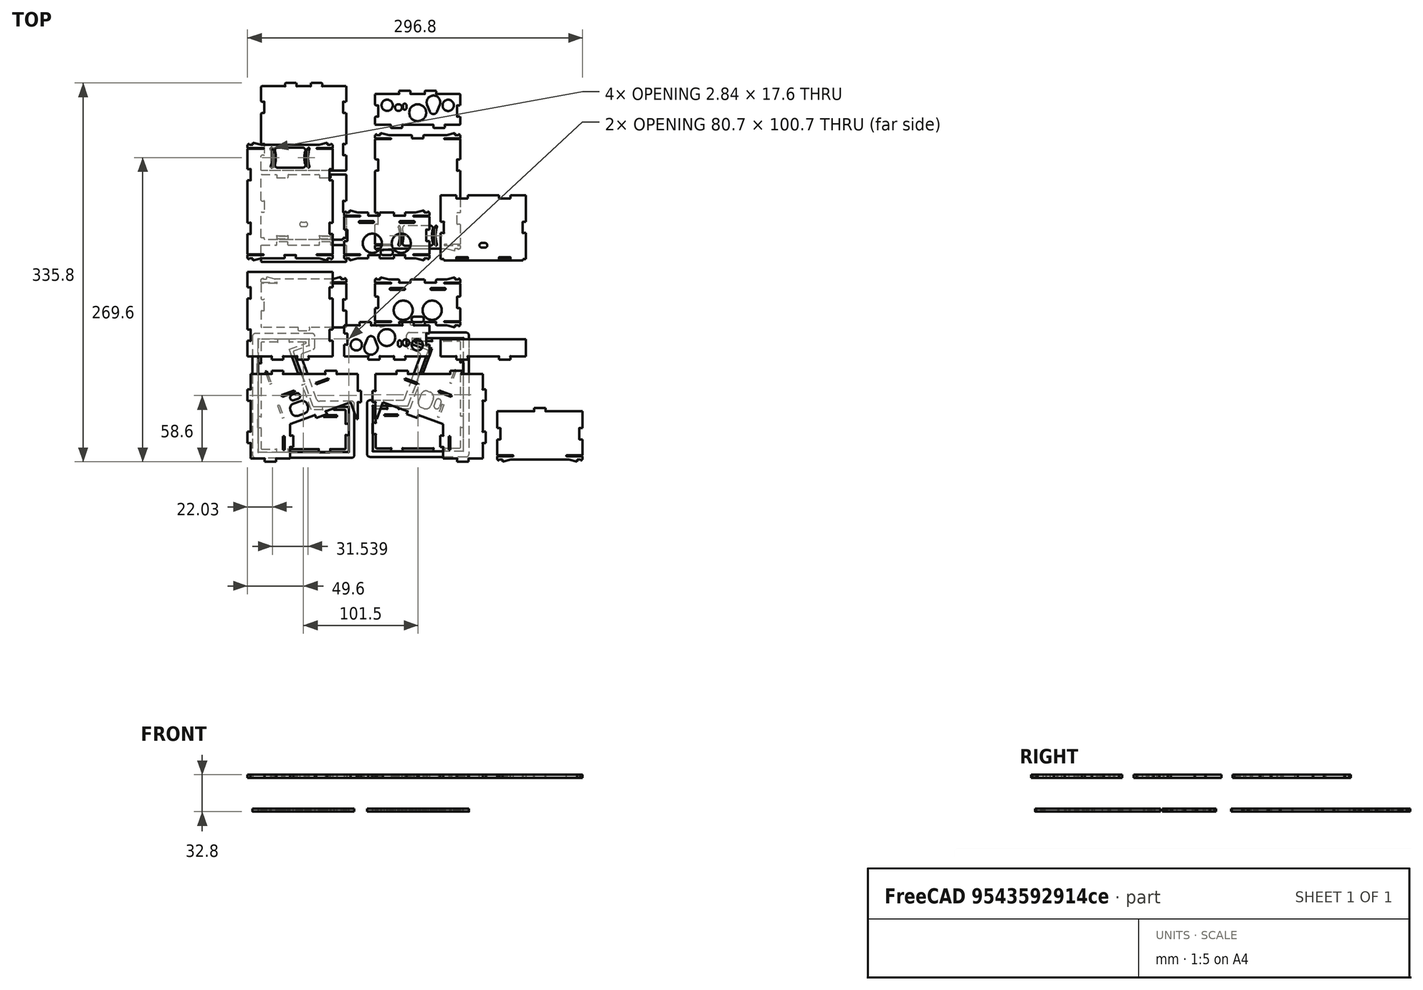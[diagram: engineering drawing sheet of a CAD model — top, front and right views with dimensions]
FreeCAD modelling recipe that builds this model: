
FCSTD DOCUMENT  (FreeCAD 1.0R39285 (Git))
Label: TheThing_v8_tabs_export_fix
License: CERN Open Hardware Licence permissive
LicenseURL: https://cern-ohl.web.cern.ch/
objects: Part::Part2DObjectPython×24, Part::Feature×11, Sketcher::SketchObject×10, Part::Chamfer×9, App::DocumentObjectGroup×2
note: 64 computed .brp shape members not serialized (recipe doc carries the construction recipe); baked Part::Feature solids carry a one-line shape summary decoded from their .brp

FEATURE [Part::Feature] test
  Placement = pos=(37.4,60.5,67.8) rot=(0,1,0;1.5708rad)
  shape: bbox 100.6 x 80.6 x 2.8 mm, 82 faces (baked)
FEATURE [Part::Feature] test001
  Placement = pos=(173.8,60.5,67.8) rot=(0,-1,0;1.5708rad)
  shape: bbox 100.6 x 80.6 x 2.8 mm, 70 faces (baked)
FEATURE [Part::Feature] test002
  Placement = pos=(259,27.5,93.2) rot=(0,-1,0;3.14159rad)
  shape: bbox 75.6 x 47.6 x 2.8 mm, 50 faces (baked)
FEATURE [Part::Feature] test003
  Placement = pos=(37.8,151.1,67.4) rot=(0,0,1;0rad)
  shape: bbox 75.6 x 77.8 x 2.8 mm, 42 faces (baked)
FEATURE [Part::Feature] test004
  Placement = pos=(123.4,151.1,33.2) rot=(0,-1,0;3.14159rad)
  shape: bbox 75.6 x 33.14 x 2.8 mm, 54 faces (baked)
FEATURE [Part::Feature] test005
  Placement = pos=(209,64.9222,78.0359) rot=(-0.34202,0,0;2.79253rad)
  shape: bbox 75.6 x 17.92 x 2.8 mm, 18 faces (baked)
FEATURE [Part::Feature] test006
  Placement = pos=(37.8,243.6,12.7) rot=(1,0,0;1.5708rad)
  shape: bbox 75.6 x 104.6 x 2.8 mm, 104 faces (baked)
FEATURE [Part::Feature] test007
  Placement = pos=(123.4,217.8,-27.7) rot=(-1,0,0;1.5708rad)
  shape: bbox 75.6 x 44.6 x 2.8 mm, 108 faces (baked)
FEATURE [Part::Feature] test008
  Placement = pos=(209,188.16,4.32219) rot=(-0.939693,0,0;1.22173rad)
  shape: bbox 75.6 x 58.11 x 2.925 mm, 56 faces (baked)
FEATURE [Part::Feature] test009
  Placement = pos=(171.3,46.5,-33) rot=(0.57735,0.57735,0.57735;4.18879rad)
  shape: bbox 90.2 x 110.2 x 2.8 mm, 46 faces (baked)
FEATURE [Part::Feature] test010
  Placement = pos=(29.4,45.7,-33) rot=(0.57735,-0.57735,-0.57735;4.18879rad)
  shape: bbox 90.2 x 110.2 x 2.8 mm, 46 faces (baked)
FEATURE [Part::Chamfer] Chamfer
  Base = -> test
  EdgeLinks = -> test [Edge25,Edge27,Edge39,Edge50,Edge52,Edge72,Edge74,Edge86,Edge97,Edge99,Edge119,Edge121,Edge133,Edge144,Edge146,Edge158,Edge169,Edge171,Edge194,Edge196]
  Edges = 20 edges r=0.5: [Edge25,Edge27,Edge39,Edge50,Edge52,Edge72,Edge74,Edge86,Edge97,Edge99,Edge119,Edge121,Edge133,Edge144,Edge146,Edge158,Edge169,Edge171,Edge194,Edge196]
  Placement = pos=(110.8,9.1,32.8) rot=(0.707107,0.707107,0;3.14159rad)
FEATURE [Part::Chamfer] Chamfer001
  Base = -> test001
  EdgeLinks = -> test001 [Edge25,Edge27,Edge39,Edge50,Edge52,Edge72,Edge74,Edge86,Edge97,Edge99,Edge119,Edge121,Edge133,Edge144,Edge146,Edge158,Edge169,Edge171,Edge194,Edge196]
  Edges = 20 edges r=0.5: [Edge25,Edge27,Edge39,Edge50,Edge52,Edge72,Edge74,Edge86,Edge97,Edge99,Edge119,Edge121,Edge133,Edge144,Edge146,Edge158,Edge169,Edge171,Edge194,Edge196]
  Placement = pos=(89.8,219.5,32.8) rot=(-0.707107,0.707107,0;3.14159rad)
FEATURE [Part::Chamfer] Chamfer002
  Base = -> test002
  EdgeLinks = -> test002 [Edge4,Edge6,Edge17,Edge20,Edge87,Edge103,Edge106,Edge120]
  Edges = 8 edges r=0.5: [Edge4,Edge6,Edge17,Edge20,Edge87,Edge103,Edge106,Edge120]
  Placement = pos=(308.8,163.8,-30) rot=(0,0,1;3.14159rad)
FEATURE [Part::Chamfer] Chamfer003
  Base = -> test003
  EdgeLinks = -> test003 [Edge1,Edge2,Edge7,Edge9,Edge27,Edge30,Edge45,Edge48,Edge59,Edge61,Edge81,Edge83,Edge95,Edge98,Edge121,Edge122]
  Edges = 16 edges r=0.5: [Edge1,Edge2,Edge7,Edge9,Edge27,Edge30,Edge45,Edge48,Edge59,Edge61,Edge81,Edge83,Edge95,Edge98,Edge121,Edge122]
  Placement = pos=(87.6,426.4,-30) rot=(0,0,1;3.14159rad)
FEATURE [Part::Chamfer] Chamfer004
  Base = -> test004
  EdgeLinks = -> test004 [Edge4,Edge7,Edge17,Edge20,Edge39,Edge42,Edge52,Edge55,Edge69,Edge73,Edge85,Edge88,Edge107,Edge110,Edge115,Edge123]
  Edges = 16 edges r=0.5: [Edge4,Edge7,Edge17,Edge20,Edge39,Edge42,Edge52,Edge55,Edge69,Edge73,Edge85,Edge88,Edge107,Edge110,Edge115,Edge123]
  Placement = pos=(274.2,419.6,-30) rot=(0,0,1;3.14159rad)
FEATURE [Part::Chamfer] Chamfer005
  Base = -> test005
  EdgeLinks = -> test005 [Edge1,Edge2,Edge5,Edge8,Edge28,Edge31,Edge50,Edge53]
  Edges = 8 edges r=0.5: [Edge1,Edge2,Edge5,Edge8,Edge28,Edge31,Edge50,Edge53]
  Placement = pos=(258.8,285.6,-30) rot=(0,0,1;3.14159rad)
FEATURE [Part::Chamfer] Chamfer006
  Base = -> test006
  EdgeLinks = -> test006 [Edge227,Edge232,Edge233,Edge238,Edge267,Edge272,Edge273,Edge278,Edge293,Edge298]
  Edges = 10 edges r=0.5: [Edge227,Edge232,Edge233,Edge238,Edge267,Edge272,Edge273,Edge278,Edge293,Edge298]
  Placement = pos=(188.6,470,-30) rot=(0,0,1;3.14159rad)
FEATURE [Part::Chamfer] Chamfer007
  Base = -> test007
  EdgeLinks = -> test007 [Edge243,Edge248,Edge249,Edge254,Edge269,Edge274,Edge289,Edge294,Edge295,Edge300,Edge315,Edge320]
  Edges = 12 edges r=0.5: [Edge243,Edge248,Edge249,Edge254,Edge269,Edge274,Edge289,Edge294,Edge295,Edge300,Edge315,Edge320]
  Placement = pos=(27.4,-59.4,-30) rot=(0,0,1;0rad)
FEATURE [Part::Chamfer] Chamfer008
  Base = -> test008
  EdgeLinks = -> test008 [Edge2,Edge4,Edge104,Edge105,Edge107,Edge118,Edge142,Edge143,Edge148,Edge149,Edge150,Edge155,Edge156,Edge164]
  Edges = 14 edges r=0.5: [Edge2,Edge4,Edge104,Edge105,Edge107,Edge118,Edge142,Edge143,Edge148,Edge149,Edge150,Edge155,Edge156,Edge164]
  Placement = pos=(-159.2,18.6,-30) rot=(0,0,1;0rad)
FEATURE [Sketcher::SketchObject] Sketch
  ArcFitTolerance = 1e-06
  FullyConstrained = true
  MakeInternals = false
  sketch-geometry (52):
    g0: LineSegment StartX=5 StartY=0 StartZ=0 EndX=95 EndY=0 EndZ=0
    g1: LineSegment StartX=100 StartY=5 StartZ=0 EndX=100 EndY=165 EndZ=0
    g2: LineSegment StartX=95 StartY=170 StartZ=0 EndX=5 EndY=170 EndZ=0
    g3: LineSegment StartX=0 StartY=165 StartZ=0 EndX=0 EndY=5 EndZ=0
    g4: LineSegment StartX=5 StartY=171 StartZ=0 EndX=95 EndY=171 EndZ=0
    g5: LineSegment StartX=100 StartY=176 StartZ=0 EndX=100 EndY=336 EndZ=0
    g6: LineSegment StartX=95 StartY=341 StartZ=0 EndX=5 EndY=341 EndZ=0
    g7: LineSegment StartX=0 StartY=336 StartZ=0 EndX=0 EndY=176 EndZ=0
    g8: LineSegment StartX=106 StartY=171 StartZ=0 EndX=196 EndY=171 EndZ=0
    g9: LineSegment StartX=201 StartY=176 StartZ=0 EndX=201 EndY=336 EndZ=0
    g10: LineSegment StartX=196 StartY=341 StartZ=0 EndX=106 EndY=341 EndZ=0
    g11: LineSegment StartX=101 StartY=336 StartZ=0 EndX=101 EndY=176 EndZ=0
    g12: LineSegment StartX=106 StartY=0 StartZ=0 EndX=196 EndY=0 EndZ=0
    g13: LineSegment StartX=201 StartY=5 StartZ=0 EndX=201 EndY=165 EndZ=0
    g14: LineSegment StartX=196 StartY=170 StartZ=0 EndX=106 EndY=170 EndZ=0
    g15: LineSegment StartX=101 StartY=165 StartZ=0 EndX=101 EndY=5 EndZ=0
    g16: LineSegment [constr] StartX=100 StartY=170 StartZ=0 EndX=101 EndY=170 EndZ=0
    g17: LineSegment [constr] StartX=101 StartY=170 StartZ=0 EndX=101 EndY=171 EndZ=0
    g18: LineSegment [constr] StartX=101 StartY=171 StartZ=0 EndX=100 EndY=171 EndZ=0
    g19: LineSegment [constr] StartX=100 StartY=171 StartZ=0 EndX=100 EndY=170 EndZ=0
    g20: ArcOfCircle CenterX=5 CenterY=5 CenterZ=0 NormalX=0 NormalY=0 NormalZ=1 AngleXU=0 Radius=5 StartAngle=3.14159 EndAngle=4.71239
    g21: GeomPoint [constr] X=0 Y=0 Z=0
    g22: ArcOfCircle CenterX=95 CenterY=5 CenterZ=0 NormalX=0 NormalY=0 NormalZ=1 AngleXU=0 Radius=5 StartAngle=4.71239 EndAngle=6.28319
    g23: GeomPoint [constr] X=100 Y=0 Z=0
    g24: ArcOfCircle CenterX=106 CenterY=5 CenterZ=0 NormalX=0 NormalY=0 NormalZ=1 AngleXU=0 Radius=5 StartAngle=3.14159 EndAngle=4.71239
    g25: GeomPoint [constr] X=101 Y=0 Z=0
    g26: ArcOfCircle CenterX=196 CenterY=5 CenterZ=0 NormalX=0 NormalY=0 NormalZ=1 AngleXU=0 Radius=5 StartAngle=4.71239 EndAngle=6.28319
    g27: GeomPoint [constr] X=201 Y=0 Z=0
    g28: ArcOfCircle CenterX=95 CenterY=176 CenterZ=0 NormalX=0 NormalY=0 NormalZ=1 AngleXU=0 Radius=5 StartAngle=4.71239 EndAngle=6.28319
    g29: GeomPoint [constr] X=100 Y=171 Z=0
    g30: ArcOfCircle CenterX=95 CenterY=165 CenterZ=0 NormalX=0 NormalY=0 NormalZ=1 AngleXU=0 Radius=5 StartAngle=3e-16 EndAngle=1.5708
    g31: GeomPoint [constr] X=100 Y=170 Z=0
    g32: ArcOfCircle CenterX=106 CenterY=165 CenterZ=0 NormalX=0 NormalY=0 NormalZ=1 AngleXU=0 Radius=5 StartAngle=1.5708 EndAngle=3.14159
    g33: GeomPoint [constr] X=101 Y=170 Z=0
    g34: ArcOfCircle CenterX=106 CenterY=176 CenterZ=0 NormalX=0 NormalY=0 NormalZ=1 AngleXU=0 Radius=5 StartAngle=3.14159 EndAngle=4.71239
    g35: GeomPoint [constr] X=101 Y=171 Z=0
    g36: ArcOfCircle CenterX=5 CenterY=176 CenterZ=0 NormalX=0 NormalY=0 NormalZ=1 AngleXU=0 Radius=5 StartAngle=3.14159 EndAngle=4.71239
    g37: GeomPoint [constr] X=0 Y=171 Z=0
    g38: ArcOfCircle CenterX=196 CenterY=176 CenterZ=0 NormalX=0 NormalY=0 NormalZ=1 AngleXU=0 Radius=5 StartAngle=4.71239 EndAngle=6.28319
    g39: GeomPoint [constr] X=201 Y=171 Z=0
    g40: ArcOfCircle CenterX=196 CenterY=165 CenterZ=0 NormalX=0 NormalY=0 NormalZ=1 AngleXU=0 Radius=5 StartAngle=2.4e-15 EndAngle=1.5708
    g41: GeomPoint [constr] X=201 Y=170 Z=0
    g42: ArcOfCircle CenterX=5 CenterY=165 CenterZ=0 NormalX=0 NormalY=0 NormalZ=1 AngleXU=0 Radius=5 StartAngle=1.5708 EndAngle=3.14159
    g43: GeomPoint [constr] X=0 Y=170 Z=0
    g44: ArcOfCircle CenterX=5 CenterY=336 CenterZ=0 NormalX=0 NormalY=0 NormalZ=1 AngleXU=0 Radius=5 StartAngle=1.5708 EndAngle=3.14159
    g45: GeomPoint [constr] X=0 Y=341 Z=0
    g46: ArcOfCircle CenterX=95 CenterY=336 CenterZ=0 NormalX=0 NormalY=0 NormalZ=1 AngleXU=0 Radius=5 StartAngle=1.7e-15 EndAngle=1.5708
    g47: GeomPoint [constr] X=100 Y=341 Z=0
    g48: ArcOfCircle CenterX=106 CenterY=336 CenterZ=0 NormalX=0 NormalY=0 NormalZ=1 AngleXU=0 Radius=5 StartAngle=1.5708 EndAngle=3.14159
    g49: GeomPoint [constr] X=101 Y=341 Z=0
    g50: ArcOfCircle CenterX=196 CenterY=336 CenterZ=0 NormalX=0 NormalY=0 NormalZ=1 AngleXU=0 Radius=5 StartAngle=-2.7e-15 EndAngle=1.5708
    g51: GeomPoint [constr] X=201 Y=341 Z=0
  constraints (119):
    c: Horizontal(g0)
    c: Horizontal(g2)
    c: Vertical(g1)
    c: Vertical(g3)
    c: Coincident(g21,g-1)
    c: Horizontal(g4)
    c: Horizontal(g6)
    c: Vertical(g5)
    c: Vertical(g7)
    c: Horizontal(g8)
    c: Horizontal(g10)
    c: Vertical(g9)
    c: Vertical(g11)
    c: Horizontal(g12)
    c: Horizontal(g14)
    c: Vertical(g13)
    c: Vertical(g15)
    c: DistanceX(g21,g23) = 100
    c: DistanceY(g21,g43) = 170
    c: Coincident(g16,g17)
    c: Coincident(g17,g18)
    c: Coincident(g18,g19)
    c: Coincident(g19,g16)
    c: Horizontal(g16)
    c: Horizontal(g18)
    c: Vertical(g17)
    c: Vertical(g19)
    c: Distance(g17,g19) = 1
    c: Distance(g16,g18) = 1
    c: Coincident(g16,g31)
    c: Coincident(g18,g29)
    c: Coincident(g17,g35)
    c: Coincident(g16,g33)
    c: PointOnObject(g21,g0)
    c: PointOnObject(g21,g3)
    c: Tangent(g0,g20) = -1.5708
    c: Tangent(g3,g20) = -1.5708
    c: PointOnObject(g23,g0)
    c: PointOnObject(g23,g1)
    c: Tangent(g0,g22) = -1.5708
    c: Tangent(g1,g22) = -1.5708
    c: PointOnObject(g25,g12)
    c: PointOnObject(g25,g15)
    c: Tangent(g12,g24) = -1.5708
    c: Tangent(g15,g24) = -1.5708
    c: PointOnObject(g27,g13)
    c: PointOnObject(g27,g12)
    c: Tangent(g13,g26) = -1.5708
    c: Tangent(g12,g26) = -1.5708
    c: PointOnObject(g29,g5)
    c: PointOnObject(g29,g4)
    c: Tangent(g5,g28) = -1.5708
    c: Tangent(g4,g28) = -1.5708
    c: PointOnObject(g31,g2)
    c: PointOnObject(g31,g1)
    c: Tangent(g2,g30) = -1.5708
    c: Tangent(g1,g30) = -1.5708
    c: PointOnObject(g33,g14)
    c: PointOnObject(g33,g15)
    c: Tangent(g14,g32) = -1.5708
    c: Tangent(g15,g32) = -1.5708
    c: PointOnObject(g35,g8)
    c: PointOnObject(g35,g11)
    c: Tangent(g8,g34) = -1.5708
    c: Tangent(g11,g34) = -1.5708
    c: PointOnObject(g37,g4)
    c: PointOnObject(g37,g7)
    c: Tangent(g4,g36) = -1.5708
    c: Tangent(g7,g36) = -1.5708
    c: PointOnObject(g39,g8)
    c: PointOnObject(g39,g9)
    c: Tangent(g8,g38) = -1.5708
    c: Tangent(g9,g38) = -1.5708
    c: PointOnObject(g41,g14)
    c: PointOnObject(g41,g13)
    c: Tangent(g14,g40) = -1.5708
    c: Tangent(g13,g40) = -1.5708
    c: PointOnObject(g43,g2)
    c: PointOnObject(g43,g3)
    c: Tangent(g2,g42) = -1.5708
    c: Tangent(g3,g42) = -1.5708
    c: PointOnObject(g45,g6)
    c: PointOnObject(g45,g7)
    c: Tangent(g6,g44) = -1.5708
    c: Tangent(g7,g44) = -1.5708
    c: PointOnObject(g47,g6)
    c: PointOnObject(g47,g5)
    c: Tangent(g6,g46) = -1.5708
    c: Tangent(g5,g46) = -1.5708
    c: PointOnObject(g49,g10)
    c: PointOnObject(g49,g11)
    c: Tangent(g10,g48) = -1.5708
    c: Tangent(g11,g48) = -1.5708
    c: PointOnObject(g51,g10)
    c: PointOnObject(g51,g9)
    c: Tangent(g10,g50) = -1.5708
    c: Tangent(g9,g50) = -1.5708
    c: Equal(g50,g48)
    c: Equal(g48,g46)
    c: Equal(g46,g44)
    c: Equal(g44,g36)
    c: Equal(g36,g42)
    c: Equal(g42,g28)
    c: Equal(g28,g34)
    c: Equal(g34,g32)
    c: Equal(g32,g30)
    c: Equal(g30,g38)
    c: Equal(g38,g40)
    c: Equal(g40,g26)
    c: Equal(g26,g24)
    c: Equal(g24,g22)
    c: Equal(g22,g20)
    c: Radius(g20) = 5
    c: Vertical(g37,g43)
    c: Horizontal(g25,g23)
    c: Vertical(g39,g41)
    c: Horizontal(g47,g49)
    c: Equal(g7,g3)
    c: Equal(g6,g10)
FEATURE [Part::Part2DObjectPython] Shape2DView  # Draft 2D object (typed FeaturePython)
  AutoUpdate = true
  Clip = false
  FuseArch = false
  HiddenLines = false
  InPlace = true
  OnlySolids = false
  Placement = pos=(96,354,3) rot=(0,0,1;1.5708rad)
  Projection = (-0.0061258,0.0189136,0.999802)
  ProjectionMode = 0
  SegmentLength = 0.05
  Tessellation = false
  VisibleOnly = false
FEATURE [Part::Part2DObjectPython] Shape2DView001  # Draft 2D object (typed FeaturePython)
  AutoUpdate = true
  Clip = false
  FuseArch = false
  HiddenLines = false
  InPlace = true
  OnlySolids = false
  Placement = pos=(138,7,3) rot=(0,0,1;3.14159rad)
  Projection = (0,0,1)
  ProjectionMode = 0
  SegmentLength = 0.05
  Tessellation = false
  VisibleOnly = false
FEATURE [Part::Part2DObjectPython] Shape2DView002  # Draft 2D object (typed FeaturePython)
  AutoUpdate = true
  Base = -> Chamfer008
  Clip = false
  FuseArch = false
  HiddenLines = false
  InPlace = true
  OnlySolids = false
  Projection = (0,0,1)
  ProjectionMode = 0
  SegmentLength = 0.05
  Tessellation = false
  VisibleOnly = false
FEATURE [Sketcher::SketchObject] Sketch001
  ArcFitTolerance = 1e-06
  FullyConstrained = false
  MakeInternals = false
  sketch-geometry (78):
    g0: LineSegment StartX=12.5 StartY=254.796 StartZ=0 EndX=25.425 EndY=254.796 EndZ=0
    g1: LineSegment StartX=14.8 StartY=198.4 StartZ=0 EndX=12.5 EndY=198.4 EndZ=0
    g2: LineSegment StartX=12.5 StartY=198.4 StartZ=0 EndX=12 EndY=198.9 EndZ=0
    g3: LineSegment StartX=14.8 StartY=197.5 StartZ=0 EndX=14.8 EndY=198.4 EndZ=0
    g4: LineSegment StartX=12 StartY=198.9 StartZ=0 EndX=12 EndY=220.843 EndZ=0
    g5: LineSegment StartX=14.8 StartY=197.5 StartZ=0 EndX=15.3 EndY=197 EndZ=0
    g6: LineSegment StartX=12.5 StartY=221.343 StartZ=0 EndX=12 EndY=220.843 EndZ=0
    g7: LineSegment StartX=25.4273 StartY=197.002 StartZ=0 EndX=15.3 EndY=197.002 EndZ=0
    g8: LineSegment StartX=12.5 StartY=221.343 StartZ=0 EndX=14.5913 EndY=221.343 EndZ=0
    g9: ArcOfCircle CenterX=14.7648 CenterY=221.443 CenterZ=0 NormalX=0 NormalY=0 NormalZ=1 AngleXU=0 Radius=0.200333 StartAngle=3.66519 EndAngle=6.28319
    g10: LineSegment StartX=25.925 StartY=199.585 StartZ=0 EndX=25.925 EndY=197.5 EndZ=0
    g11: ArcOfCircle CenterX=14.7648 CenterY=221.443 CenterZ=0 NormalX=0 NormalY=0 NormalZ=1 AngleXU=0 Radius=0.200333 StartAngle=0 EndAngle=1.0472
    g12: ArcOfEllipse CenterX=26.0227 CenterY=199.765 CenterZ=0 NormalX=0 NormalY=0 NormalZ=1 MajorRadius=0.207869 MinorRadius=0.195333 AngleXU=1.5708 StartAngle=1.5708 EndAngle=2.61799
    g13: ArcOfEllipse CenterX=26.0227 CenterY=199.765 CenterZ=0 NormalX=0 NormalY=0 NormalZ=1 MajorRadius=0.207869 MinorRadius=0.195333 AngleXU=1.5708 StartAngle=5.23599 EndAngle=7.85398
    g14: LineSegment StartX=14.865 StartY=231.019 StartZ=0 EndX=14.865 EndY=221.616 EndZ=0
    g15: LineSegment StartX=35.6082 StartY=199.869 StartZ=0 EndX=26.1918 EndY=199.869 EndZ=0
    g16: ArcOfCircle CenterX=14.7648 CenterY=231.192 CenterZ=0 NormalX=0 NormalY=0 NormalZ=1 AngleXU=0 Radius=0.200333 StartAngle=5.23599 EndAngle=6.28319
    g17: ArcOfEllipse CenterX=35.7773 CenterY=199.765 CenterZ=0 NormalX=0 NormalY=0 NormalZ=1 MajorRadius=0.207869 MinorRadius=0.195333 AngleXU=1.5708 StartAngle=4.71239 EndAngle=7.33038
    g18: ArcOfEllipse CenterX=35.7773 CenterY=199.765 CenterZ=0 NormalX=0 NormalY=0 NormalZ=1 MajorRadius=0.207869 MinorRadius=0.195333 AngleXU=1.5708 StartAngle=3.66519 EndAngle=4.71239
    g19: ArcOfCircle CenterX=14.7648 CenterY=231.192 CenterZ=0 NormalX=0 NormalY=0 NormalZ=1 AngleXU=0 Radius=0.200333 StartAngle=0 EndAngle=2.61799
    g20: LineSegment StartX=35.875 StartY=199.585 StartZ=0 EndX=35.875 EndY=197.5 EndZ=0
    g21: LineSegment StartX=12.5 StartY=231.293 StartZ=0 EndX=14.5913 EndY=231.293 EndZ=0
    g22: LineSegment StartX=12 StartY=231.793 StartZ=0 EndX=12.5 EndY=231.293 EndZ=0
    g23: LineSegment StartX=63.2283 StartY=197.003 StartZ=0 EndX=36.3717 EndY=197.003 EndZ=0
    g24: LineSegment StartX=12.5 StartY=254.796 StartZ=0 EndX=12 EndY=254.296 EndZ=0
    g25: LineSegment StartX=63.725 StartY=199.585 StartZ=0 EndX=63.725 EndY=197.5 EndZ=0
    g26: ArcOfEllipse CenterX=63.8227 CenterY=199.765 CenterZ=0 NormalX=0 NormalY=0 NormalZ=1 MajorRadius=0.207869 MinorRadius=0.195333 AngleXU=1.5708 StartAngle=1.5708 EndAngle=2.61799
    g27: ArcOfEllipse CenterX=63.8227 CenterY=199.765 CenterZ=0 NormalX=0 NormalY=0 NormalZ=1 MajorRadius=0.207869 MinorRadius=0.195333 AngleXU=1.5708 StartAngle=5.23599 EndAngle=7.85398
    g28: LineSegment StartX=25.425 StartY=254.796 StartZ=0 EndX=25.925 EndY=254.296 EndZ=0
    g29: LineSegment StartX=73.4082 StartY=199.869 StartZ=0 EndX=63.9918 EndY=199.869 EndZ=0
    g30: LineSegment StartX=25.925 StartY=254.296 StartZ=0 EndX=25.925 EndY=252.204 EndZ=0
    g31: ArcOfEllipse CenterX=73.5773 CenterY=199.765 CenterZ=0 NormalX=0 NormalY=0 NormalZ=1 MajorRadius=0.207869 MinorRadius=0.195333 AngleXU=1.5708 StartAngle=4.71239 EndAngle=7.33038
    g32: ArcOfEllipse CenterX=73.5773 CenterY=199.765 CenterZ=0 NormalX=0 NormalY=0 NormalZ=1 MajorRadius=0.207869 MinorRadius=0.195333 AngleXU=1.5708 StartAngle=3.66519 EndAngle=4.71239
    g33: ArcOfCircle CenterX=26.0252 CenterY=252.031 CenterZ=0 NormalX=0 NormalY=0 NormalZ=1 AngleXU=-1.5708 Radius=0.200333 StartAngle=3.66519 EndAngle=6.28319
    g34: LineSegment StartX=73.675 StartY=199.585 StartZ=0 EndX=73.675 EndY=197.5 EndZ=0
    g35: ArcOfCircle CenterX=26.0252 CenterY=252.031 CenterZ=0 NormalX=0 NormalY=0 NormalZ=1 AngleXU=-1.5708 Radius=0.200333 StartAngle=0 EndAngle=1.0472
    g36: LineSegment StartX=26.1987 StartY=251.931 StartZ=0 EndX=35.6013 EndY=251.931 EndZ=0
    g37: LineSegment StartX=84.3 StartY=196.999 StartZ=0 EndX=74.1757 EndY=196.999 EndZ=0
    g38: ArcOfCircle CenterX=35.7748 CenterY=252.031 CenterZ=0 NormalX=0 NormalY=0 NormalZ=1 AngleXU=-1.5708 Radius=0.200333 StartAngle=5.23599 EndAngle=6.28319
    g39: LineSegment StartX=84.3 StartY=197 StartZ=0 EndX=84.8 EndY=197.5 EndZ=0
    g40: ArcOfCircle CenterX=35.7748 CenterY=252.031 CenterZ=0 NormalX=0 NormalY=0 NormalZ=1 AngleXU=-1.5708 Radius=0.200333 StartAngle=0 EndAngle=2.61799
    g41: LineSegment StartX=84.8 StartY=198.4 StartZ=0 EndX=84.8 EndY=197.5 EndZ=0
    g42: LineSegment StartX=35.875 StartY=254.296 StartZ=0 EndX=35.875 EndY=252.204 EndZ=0
    g43: LineSegment StartX=87.1 StartY=198.4 StartZ=0 EndX=84.8 EndY=198.4 EndZ=0
    g44: LineSegment StartX=36.375 StartY=254.796 StartZ=0 EndX=35.875 EndY=254.296 EndZ=0
    g45: LineSegment StartX=87.1 StartY=198.4 StartZ=0 EndX=87.6 EndY=198.9 EndZ=0
    g46: LineSegment StartX=36.375 StartY=254.796 StartZ=0 EndX=63.225 EndY=254.796 EndZ=0
    g47: LineSegment StartX=87.6 StartY=220.843 StartZ=0 EndX=87.6 EndY=198.9 EndZ=0
    g48: LineSegment StartX=63.725 StartY=254.296 StartZ=0 EndX=63.225 EndY=254.796 EndZ=0
    g49: LineSegment StartX=87.6 StartY=220.843 StartZ=0 EndX=87.1 EndY=221.343 EndZ=0
    g50: LineSegment StartX=63.725 StartY=254.296 StartZ=0 EndX=63.725 EndY=252.204 EndZ=0
    g51: LineSegment StartX=85.0087 StartY=221.343 StartZ=0 EndX=87.1 EndY=221.343 EndZ=0
    g52: ArcOfCircle CenterX=63.8252 CenterY=252.031 CenterZ=0 NormalX=0 NormalY=0 NormalZ=1 AngleXU=-1.5708 Radius=0.200333 StartAngle=3.66519 EndAngle=6.28319
    g53: ArcOfCircle CenterX=84.8352 CenterY=221.443 CenterZ=0 NormalX=0 NormalY=0 NormalZ=1 AngleXU=0 Radius=0.200333 StartAngle=2.0944 EndAngle=5.75959
    g54: ArcOfCircle CenterX=63.8252 CenterY=252.031 CenterZ=0 NormalX=0 NormalY=0 NormalZ=1 AngleXU=-1.5708 Radius=0.200333 StartAngle=0 EndAngle=1.0472
    g55: LineSegment StartX=84.735 StartY=231.019 StartZ=0 EndX=84.735 EndY=221.616 EndZ=0
    g56: LineSegment StartX=63.9987 StartY=251.931 StartZ=0 EndX=73.4013 EndY=251.931 EndZ=0
    g57: ArcOfCircle CenterX=84.8352 CenterY=231.192 CenterZ=0 NormalX=0 NormalY=0 NormalZ=1 AngleXU=0 Radius=0.200333 StartAngle=0.523599 EndAngle=4.18879
    g58: ArcOfCircle CenterX=73.5748 CenterY=252.031 CenterZ=0 NormalX=0 NormalY=0 NormalZ=1 AngleXU=-1.5708 Radius=0.200333 StartAngle=5.23599 EndAngle=6.28319
    g59: LineSegment StartX=85.0087 StartY=231.293 StartZ=0 EndX=87.1 EndY=231.293 EndZ=0
    g60: ArcOfCircle CenterX=73.5748 CenterY=252.031 CenterZ=0 NormalX=0 NormalY=0 NormalZ=1 AngleXU=-1.5708 Radius=0.200333 StartAngle=0 EndAngle=2.61799
    g61: LineSegment StartX=87.1 StartY=231.293 StartZ=0 EndX=87.6 EndY=231.793 EndZ=0
    g62: LineSegment StartX=73.675 StartY=254.296 StartZ=0 EndX=73.675 EndY=252.204 EndZ=0
    g63: LineSegment StartX=74.175 StartY=254.796 StartZ=0 EndX=73.675 EndY=254.296 EndZ=0
    g64: LineSegment StartX=87.6 StartY=254.296 StartZ=0 EndX=87.1 EndY=254.796 EndZ=0
    g65: LineSegment StartX=74.175 StartY=254.796 StartZ=0 EndX=87.1 EndY=254.796 EndZ=0
    g66: LineSegment StartX=48.3 StartY=212.512 StartZ=0 EndX=51.3 EndY=212.512 EndZ=0
    g67: ArcOfCircle CenterX=48.3 CenterY=210.512 CenterZ=0 NormalX=0 NormalY=0 NormalZ=1 AngleXU=0 Radius=2 StartAngle=1.5708 EndAngle=4.71239
    g68: ArcOfCircle CenterX=51.3 CenterY=210.512 CenterZ=0 NormalX=0 NormalY=0 NormalZ=1 AngleXU=0 Radius=2 StartAngle=4.71239 EndAngle=7.85398
    g69: LineSegment StartX=48.3 StartY=208.512 StartZ=0 EndX=51.3 EndY=208.512 EndZ=0
    g70: LineSegment StartX=12 StartY=254.296 StartZ=0 EndX=12 EndY=233.023 EndZ=0
    g71: LineSegment StartX=12 StartY=231.793 StartZ=0 EndX=12 EndY=232.027 EndZ=0
    g72: LineSegment StartX=87.6 StartY=231.793 StartZ=0 EndX=87.6 EndY=232.021 EndZ=0
    g73: LineSegment StartX=87.6 StartY=233.009 StartZ=0 EndX=87.6 EndY=254.296 EndZ=0
    g74: LineSegment StartX=25.925 StartY=197.5 StartZ=0 EndX=25.4273 EndY=197.002 EndZ=0
    g75: LineSegment StartX=35.875 StartY=197.5 StartZ=0 EndX=36.3717 EndY=197.003 EndZ=0
    g76: LineSegment StartX=63.725 StartY=197.5 StartZ=0 EndX=63.2283 EndY=197.003 EndZ=0
    g77: LineSegment StartX=73.675 StartY=197.5 StartZ=0 EndX=74.1757 EndY=196.999 EndZ=0
  constraints (32):
    c: Coincident(g70,g24)
    c: Vertical(g70)
    c: Coincident(g71,g22)
    c: Vertical(g71)
    c: Coincident(g11,g14)
    c: Vertical(g55)
    c: Vertical(g14)
    c: Coincident(g72,g61)
    c: Vertical(g72)
    c: Coincident(g73,g64)
    c: Vertical(g73)
    c: Horizontal(g7)
    c: Vertical(g10)
    c: Vertical(g20)
    c: Horizontal(g23)
    c: Vertical(g25)
    c: Vertical(g34)
    c: Horizontal(g37)
    c: DistanceX(g3) = 14.8
    c: DistanceY(g3) = 197.5
    c: Angle(g-1,g74) = -2.35619
    c: Angle(g-1,g75) = -0.785398
    c: Angle(g-1,g76) = -2.35619
    c: Angle(g-1,g77) = -0.785398
    c: Coincident(g23,g76)
    c: PointOnObject(g25,g76)
    c: Coincident(g37,g77)
    c: Coincident(g34,g77)
    c: PointOnObject(g20,g75)
    c: Coincident(g23,g75)
    c: Coincident(g7,g74)
    c: Coincident(g10,g74)
FEATURE [Part::Part2DObjectPython] Shape2DView003  # Draft 2D object (typed FeaturePython)
  AutoUpdate = true
  Base = -> test009
  Clip = false
  FuseArch = false
  HiddenLines = false
  InPlace = true
  OnlySolids = false
  Projection = (0,0,1)
  ProjectionMode = 0
  SegmentLength = 0.05
  Tessellation = false
  VisibleOnly = false
FEATURE [Part::Part2DObjectPython] Shape2DView004  # Draft 2D object (typed FeaturePython)
  AutoUpdate = true
  Base = -> test010
  Clip = false
  FuseArch = false
  HiddenLines = false
  InPlace = true
  OnlySolids = false
  Placement = pos=(0,1,0) rot=(0,0,1;0rad)
  Projection = (0,0,1)
  ProjectionMode = 0
  SegmentLength = 0.05
  Tessellation = false
  VisibleOnly = false
FEATURE [Part::Part2DObjectPython] Shape2DView005  # Draft 2D object (typed FeaturePython)
  AutoUpdate = true
  Base = -> Chamfer
  Clip = false
  FuseArch = false
  HiddenLines = false
  InPlace = true
  OnlySolids = false
  Projection = (0,0,1)
  ProjectionMode = 0
  SegmentLength = 0.05
  Tessellation = false
  VisibleOnly = false
FEATURE [Part::Part2DObjectPython] Shape2DView006  # Draft 2D object (typed FeaturePython)
  AutoUpdate = true
  Base = -> Chamfer001
  Clip = false
  FuseArch = false
  HiddenLines = false
  InPlace = true
  OnlySolids = false
  Placement = pos=(0,1,0) rot=(0,0,1;0rad)
  Projection = (0,0,1)
  ProjectionMode = 0
  SegmentLength = 0.05
  Tessellation = false
  VisibleOnly = false
FEATURE [Part::Part2DObjectPython] Shape2DView007  # Draft 2D object (typed FeaturePython)
  AutoUpdate = true
  Base = -> Chamfer002
  Clip = false
  FuseArch = false
  HiddenLines = false
  InPlace = true
  OnlySolids = false
  Projection = (0,0,1)
  ProjectionMode = 0
  SegmentLength = 0.05
  Tessellation = false
  VisibleOnly = false
FEATURE [Part::Part2DObjectPython] Shape2DView008  # Draft 2D object (typed FeaturePython)
  AutoUpdate = true
  Base = -> Chamfer003
  Clip = false
  FuseArch = false
  HiddenLines = false
  InPlace = true
  OnlySolids = false
  Projection = (0,0,1)
  ProjectionMode = 0
  SegmentLength = 0.05
  Tessellation = false
  VisibleOnly = false
FEATURE [Part::Part2DObjectPython] Shape2DView009  # Draft 2D object (typed FeaturePython)
  AutoUpdate = true
  Base = -> Chamfer004
  Clip = false
  FuseArch = false
  HiddenLines = false
  InPlace = true
  OnlySolids = false
  Projection = (0,0,1)
  ProjectionMode = 0
  SegmentLength = 0.05
  Tessellation = false
  VisibleOnly = false
FEATURE [Part::Part2DObjectPython] Shape2DView010  # Draft 2D object (typed FeaturePython)
  AutoUpdate = true
  Base = -> Chamfer005
  Clip = false
  FuseArch = false
  HiddenLines = false
  InPlace = true
  OnlySolids = false
  Projection = (0,0,1)
  ProjectionMode = 0
  SegmentLength = 0.05
  Tessellation = false
  VisibleOnly = false
FEATURE [Part::Part2DObjectPython] Shape2DView011  # Draft 2D object (typed FeaturePython)
  AutoUpdate = true
  Base = -> Chamfer006
  Clip = false
  FuseArch = false
  HiddenLines = false
  InPlace = true
  OnlySolids = false
  Projection = (0,0,1)
  ProjectionMode = 0
  SegmentLength = 0.05
  Tessellation = false
  VisibleOnly = false
FEATURE [Part::Part2DObjectPython] Shape2DView012  # Draft 2D object (typed FeaturePython)
  AutoUpdate = true
  Base = -> Chamfer007
  Clip = false
  FuseArch = false
  HiddenLines = false
  InPlace = true
  OnlySolids = false
  Projection = (0,0,1)
  ProjectionMode = 0
  SegmentLength = 0.05
  Tessellation = false
  VisibleOnly = false
FEATURE [App::DocumentObjectGroup] Group  label="Incoming_Solids"
  Group = -> [test009,test010,Chamfer,Chamfer001,Chamfer002,Chamfer003,Chamfer004,Chamfer005,Chamfer006,Chamfer007,Chamfer008,Shape2DView002,Shape2DView003,Shape2DView004,Shape2DView005,Shape2DView006,Shape2DView007,Shape2DView008,Shape2DView009,Shape2DView010,Shape2DView011,Shape2DView012]
FEATURE [Part::Part2DObjectPython] ShapeString  # Draft 2D object (typed FeaturePython)
  FontFile = <userpath>/Downloads/fonts/Droid_Sans_Mono/DroidSansMono.ttf
  Fuse = false
  Justification = 6
  JustificationReference = 0
  KeepLeftMargin = false
  MakeFace = true
  ObliqueAngle = 0
  Placement = pos=(166,103,0) rot=(0,0,1;0rad)
  ScaleToSize = true
  Size = 2.5
  String = [1]
  Tracking = 0
FEATURE [Part::Part2DObjectPython] ShapeString001  # Draft 2D object (typed FeaturePython)
  FontFile = <userpath>/Downloads/fonts/Droid_Sans_Mono/DroidSansMono.ttf
  Fuse = false
  Justification = 6
  JustificationReference = 0
  KeepLeftMargin = false
  MakeFace = true
  ObliqueAngle = 0
  Placement = pos=(29,103,0) rot=(0,0,1;0rad)
  ScaleToSize = true
  Size = 2.5
  String = [2]
  Tracking = 0
FEATURE [Part::Part2DObjectPython] ShapeString002  # Draft 2D object (typed FeaturePython)
  FontFile = <userpath>/Downloads/fonts/Droid_Sans_Mono/DroidSansMono.ttf
  Fuse = false
  Justification = 6
  JustificationReference = 0
  KeepLeftMargin = false
  MakeFace = true
  ObliqueAngle = 0
  Placement = pos=(148,283,0) rot=(0,0,1;0rad)
  ScaleToSize = true
  Size = 2.5
  String = [3]
  Tracking = 0
FEATURE [Part::Part2DObjectPython] ShapeString003  # Draft 2D object (typed FeaturePython)
  FontFile = <userpath>/Downloads/fonts/Droid_Sans_Mono/DroidSansMono.ttf
  Fuse = false
  Justification = 6
  JustificationReference = 0
  KeepLeftMargin = false
  MakeFace = true
  ObliqueAngle = 0
  Placement = pos=(47,248,0) rot=(0,0,1;0rad)
  ScaleToSize = true
  Size = 2.5
  String = [4]
  Tracking = 0
FEATURE [Part::Part2DObjectPython] ShapeString004  # Draft 2D object (typed FeaturePython)
  FontFile = <userpath>/Downloads/fonts/Droid_Sans_Mono/DroidSansMono.ttf
  Fuse = false
  Justification = 6
  JustificationReference = 0
  KeepLeftMargin = false
  MakeFace = true
  ObliqueAngle = 0
  Placement = pos=(148,322,0) rot=(0,0,1;0rad)
  ScaleToSize = true
  Size = 2.5
  String = [5]
  Tracking = 0
FEATURE [Part::Part2DObjectPython] ShapeString005  # Draft 2D object (typed FeaturePython)
  FontFile = <userpath>/Downloads/fonts/Droid_Sans_Mono/DroidSansMono.ttf
  Fuse = false
  Justification = 6
  JustificationReference = 0
  KeepLeftMargin = false
  MakeFace = true
  ObliqueAngle = 0
  Placement = pos=(148,155,0) rot=(0,0,1;0rad)
  ScaleToSize = true
  Size = 2.5
  String = [6]
  Tracking = 0
FEATURE [Part::Part2DObjectPython] ShapeString006  # Draft 2D object (typed FeaturePython)
  FontFile = <userpath>/Downloads/fonts/Droid_Sans_Mono/DroidSansMono.ttf
  Fuse = false
  Justification = 6
  JustificationReference = 0
  KeepLeftMargin = false
  MakeFace = true
  ObliqueAngle = 0
  Placement = pos=(47,329,0) rot=(0,0,1;0rad)
  ScaleToSize = true
  Size = 2.5
  String = [7]
  Tracking = 0
FEATURE [Part::Part2DObjectPython] ShapeString007  # Draft 2D object (typed FeaturePython)
  FontFile = <userpath>/Downloads/fonts/Droid_Sans_Mono/DroidSansMono.ttf
  Fuse = false
  Justification = 6
  JustificationReference = 0
  KeepLeftMargin = false
  MakeFace = true
  ObliqueAngle = 0
  Placement = pos=(47,158,0) rot=(0,0,1;0rad)
  ScaleToSize = true
  Size = 2.5
  String = [8]
  Tracking = 0
FEATURE [Part::Part2DObjectPython] ShapeString008  # Draft 2D object (typed FeaturePython)
  FontFile = <userpath>/Downloads/fonts/Droid_Sans_Mono/DroidSansMono.ttf
  Fuse = false
  Justification = 6
  JustificationReference = 0
  KeepLeftMargin = false
  MakeFace = true
  ObliqueAngle = 0
  Placement = pos=(47,188,0) rot=(0,0,1;0rad)
  ScaleToSize = true
  Size = 2.5
  String = [9]
  Tracking = 0
FEATURE [Part::Part2DObjectPython] ShapeString009  # Draft 2D object (typed FeaturePython)
  FontFile = <userpath>/Downloads/fonts/Droid_Sans_Mono/DroidSansMono.ttf
  Fuse = false
  Justification = 6
  JustificationReference = 0
  KeepLeftMargin = false
  MakeFace = true
  ObliqueAngle = 0
  Placement = pos=(166,111,0) rot=(0,0,1;0rad)
  ScaleToSize = true
  Size = 2.5
  String = [10]
  Tracking = 0
FEATURE [Part::Part2DObjectPython] ShapeString010  # Draft 2D object (typed FeaturePython)
  FontFile = <userpath>/Downloads/fonts/Droid_Sans_Mono/DroidSansMono.ttf
  Fuse = false
  Justification = 6
  JustificationReference = 0
  KeepLeftMargin = false
  MakeFace = true
  ObliqueAngle = 0
  Placement = pos=(28,111,0) rot=(0,0,1;0rad)
  ScaleToSize = true
  Size = 2.5
  String = [11]
  Tracking = 0
FEATURE [Sketcher::SketchObject] Sketch002
  ArcFitTolerance = 1e-06
  FullyConstrained = false
  MakeInternals = false
  sketch-geometry (156):
    g0: LineSegment StartX=143.5 StartY=114.5 StartZ=0 EndX=167.876 EndY=114.5 EndZ=0
    g1: ArcOfCircle CenterX=143.5 CenterY=112 CenterZ=0 NormalX=0 NormalY=0 NormalZ=1 AngleXU=1e-15 Radius=2.5 StartAngle=1.5708 EndAngle=3.14159
    g2: ArcOfCircle CenterX=193.7 CenterY=112 CenterZ=0 NormalX=0 NormalY=0 NormalZ=1 AngleXU=1e-15 Radius=2.5 StartAngle=0 EndAngle=1.5708
    g3: LineSegment StartX=141 StartY=102.631 StartZ=0 EndX=141 EndY=112 EndZ=0
    g4: LineSegment StartX=196.2 StartY=112 StartZ=0 EndX=196.2 EndY=6.8 EndZ=0
    g5: ArcOfCircle CenterX=143.5 CenterY=102.631 CenterZ=0 NormalX=0 NormalY=0 NormalZ=1 AngleXU=1e-15 Radius=2.5 StartAngle=3.14159 EndAngle=4.36332
    g6: ArcOfCircle CenterX=193.7 CenterY=6.8 CenterZ=0 NormalX=0 NormalY=0 NormalZ=1 AngleXU=1e-15 Radius=2.5 StartAngle=4.71239 EndAngle=6.28319
    g7: LineSegment StartX=151.613 StartY=97.0174 StartZ=0 EndX=142.645 EndY=100.281 EndZ=0
    g8: LineSegment StartX=193.7 StartY=4.3 StartZ=0 EndX=170.196 EndY=4.3 EndZ=0
    g9: ArcOfCircle CenterX=150.758 CenterY=94.6682 CenterZ=0 NormalX=0 NormalY=0 NormalZ=1 AngleXU=1e-15 Radius=2.5 StartAngle=5.93412 EndAngle=7.50492
    g10: ArcOfCircle CenterX=108.5 CenterY=6.8 CenterZ=0 NormalX=0 NormalY=0 NormalZ=1 AngleXU=1e-15 Radius=2.5 StartAngle=3.14159 EndAngle=4.71239
    g11: LineSegment StartX=139.397 StartY=56.1449 StartZ=0 EndX=153.107 EndY=93.8131 EndZ=0
    g12: LineSegment StartX=106 StartY=6.8 StartZ=0 EndX=106 EndY=52 EndZ=0
    g13: ArcOfCircle CenterX=137.048 CenterY=57 CenterZ=0 NormalX=0 NormalY=0 NormalZ=1 AngleXU=1e-15 Radius=2.5 StartAngle=4.71239 EndAngle=5.93412
    g14: ArcOfCircle CenterX=108.5 CenterY=52 CenterZ=0 NormalX=0 NormalY=0 NormalZ=1 AngleXU=1e-15 Radius=2.5 StartAngle=1.5708 EndAngle=3.14159
    g15: LineSegment StartX=108.5 StartY=54.5 StartZ=0 EndX=137.048 EndY=54.5 EndZ=0
    g16: ArcOfCircle CenterX=146.433 CenterY=109.75 CenterZ=0 NormalX=0 NormalY=0 NormalZ=1 AngleXU=9e-16 Radius=0.25 StartAngle=3.66519 EndAngle=4.71239
    g17: ArcOfCircle CenterX=146 CenterY=109.5 CenterZ=0 NormalX=0 NormalY=0 NormalZ=1 AngleXU=9e-16 Radius=0.25 StartAngle=0.523599 EndAngle=4.18879
    g18: ArcOfCircle CenterX=145.75 CenterY=109.067 CenterZ=0 NormalX=0 NormalY=0 NormalZ=1 AngleXU=9e-16 Radius=0.25 StartAngle=-8.9e-15 EndAngle=1.0472
    g19: LineSegment StartX=146 StartY=104.493 StartZ=0 EndX=146 EndY=109.067 EndZ=0
    g20: ArcOfCircle CenterX=145.75 CenterY=104.493 CenterZ=0 NormalX=0 NormalY=0 NormalZ=1 AngleXU=9e-16 Radius=0.25 StartAngle=5.23599 EndAngle=6.28319
    g21: ArcOfCircle CenterX=146 CenterY=104.06 CenterZ=0 NormalX=0 NormalY=0 NormalZ=1 AngleXU=9e-16 Radius=0.25 StartAngle=2.0944 EndAngle=5.41052
    g22: ArcOfCircle CenterX=146.321 CenterY=103.677 CenterZ=0 NormalX=0 NormalY=0 NormalZ=1 AngleXU=9e-16 Radius=0.25 StartAngle=1.22173 EndAngle=2.26893
    g23: LineSegment StartX=159.328 StartY=99.2094 StartZ=0 EndX=146.407 EndY=103.912 EndZ=0
    g24: ArcOfCircle CenterX=158.986 CenterY=98.2697 CenterZ=0 NormalX=0 NormalY=0 NormalZ=1 AngleXU=1e-15 Radius=1 StartAngle=5.93412 EndAngle=7.50492
    g25: LineSegment StartX=142.539 StartY=50.158 StartZ=0 EndX=159.926 EndY=97.9277 EndZ=0
    g26: ArcOfCircle CenterX=141.599 CenterY=50.5 CenterZ=0 NormalX=0 NormalY=0 NormalZ=1 AngleXU=1e-15 Radius=1 StartAngle=4.71239 EndAngle=5.93412
    g27: LineSegment StartX=111.433 StartY=49.5 StartZ=0 EndX=141.599 EndY=49.5 EndZ=0
    g28: ArcOfCircle CenterX=111.433 CenterY=49.75 CenterZ=0 NormalX=0 NormalY=0 NormalZ=1 AngleXU=9e-16 Radius=0.25 StartAngle=3.66519 EndAngle=4.71239
    g29: ArcOfCircle CenterX=111 CenterY=49.5 CenterZ=0 NormalX=0 NormalY=0 NormalZ=1 AngleXU=9e-16 Radius=0.25 StartAngle=0.523599 EndAngle=4.18879
    g30: ArcOfCircle CenterX=110.75 CenterY=49.067 CenterZ=0 NormalX=0 NormalY=0 NormalZ=1 AngleXU=9e-16 Radius=0.25 StartAngle=1e-15 EndAngle=1.0472
    g31: LineSegment StartX=111 StartY=9.73301 StartZ=0 EndX=111 EndY=49.067 EndZ=0
    g32: ArcOfCircle CenterX=110.75 CenterY=9.73301 CenterZ=0 NormalX=0 NormalY=0 NormalZ=1 AngleXU=9e-16 Radius=0.25 StartAngle=5.23599 EndAngle=6.28319
    g33: ArcOfCircle CenterX=111 CenterY=9.3 CenterZ=0 NormalX=0 NormalY=0 NormalZ=1 AngleXU=9e-16 Radius=0.25 StartAngle=2.0944 EndAngle=5.75959
    g34: ArcOfCircle CenterX=111.433 CenterY=9.05 CenterZ=0 NormalX=0 NormalY=0 NormalZ=1 AngleXU=9e-16 Radius=0.25 StartAngle=1.5708 EndAngle=2.61799
    g35: LineSegment StartX=190.767 StartY=9.3 StartZ=0 EndX=170.196 EndY=9.3 EndZ=0
    g36: ArcOfCircle CenterX=190.767 CenterY=9.05 CenterZ=0 NormalX=0 NormalY=0 NormalZ=1 AngleXU=9e-16 Radius=0.25 StartAngle=0.523599 EndAngle=1.5708
    g37: ArcOfCircle CenterX=191.2 CenterY=9.3 CenterZ=0 NormalX=0 NormalY=0 NormalZ=1 AngleXU=9e-16 Radius=0.25 StartAngle=3.66519 EndAngle=7.33038
    g38: ArcOfCircle CenterX=191.45 CenterY=9.73301 CenterZ=0 NormalX=0 NormalY=0 NormalZ=1 AngleXU=9e-16 Radius=0.25 StartAngle=3.14159 EndAngle=4.18879
    g39: LineSegment StartX=191.2 StartY=109.067 StartZ=0 EndX=191.2 EndY=9.73301 EndZ=0
    g40: ArcOfCircle CenterX=191.45 CenterY=109.067 CenterZ=0 NormalX=0 NormalY=0 NormalZ=1 AngleXU=9e-16 Radius=0.25 StartAngle=2.0944 EndAngle=3.14159
    g41: ArcOfCircle CenterX=191.2 CenterY=109.5 CenterZ=0 NormalX=0 NormalY=0 NormalZ=1 AngleXU=9e-16 Radius=0.25 StartAngle=5.23599 EndAngle=8.90118
    g42: ArcOfCircle CenterX=190.767 CenterY=109.75 CenterZ=0 NormalX=0 NormalY=0 NormalZ=1 AngleXU=9e-16 Radius=0.25 StartAngle=4.71239 EndAngle=5.75959
    g43: LineSegment StartX=146.433 StartY=109.5 StartZ=0 EndX=167.876 EndY=109.5 EndZ=0
    g44: LineSegment StartX=163.525 StartY=107.087 StartZ=0 EndX=163.525 EndY=109.2 EndZ=0
    g45: LineSegment StartX=163.525 StartY=109.2 StartZ=0 EndX=163.825 EndY=109.5 EndZ=0
    g46: ArcOfCircle CenterX=163.525 CenterY=106.9 CenterZ=0 NormalX=0 NormalY=0 NormalZ=1 AngleXU=1.5708 Radius=0.186667 StartAngle=1.5708 EndAngle=4.71239
    g47: ArcOfCircle CenterX=163.525 CenterY=106.9 CenterZ=0 NormalX=0 NormalY=0 NormalZ=1 AngleXU=1.5708 Radius=0.186667 StartAngle=4.71239 EndAngle=6.28319
    g48: LineSegment StartX=155.42 StartY=78.4934 StartZ=0 EndX=153.434 EndY=79.2163 EndZ=0
    g49: LineSegment StartX=153.05 StartY=79.0369 StartZ=0 EndX=153.434 EndY=79.2163 EndZ=0
    g50: ArcOfCircle CenterX=155.596 CenterY=78.4296 CenterZ=0 NormalX=0 NormalY=0 NormalZ=1 AngleXU=2.79253 Radius=0.186667 StartAngle=0 EndAngle=1.5708
    g51: ArcOfCircle CenterX=155.596 CenterY=78.4296 CenterZ=0 NormalX=0 NormalY=0 NormalZ=1 AngleXU=2.79253 Radius=0.186667 StartAngle=1.5708 EndAngle=4.71239
    g52: LineSegment StartX=149.963 StartY=69.6784 StartZ=0 EndX=149.784 EndY=70.0629 EndZ=0
    g53: LineSegment StartX=155.66 StartY=78.605 StartZ=0 EndX=163.6 EndY=100.421 EndZ=0
    g54: LineSegment StartX=151.949 StartY=68.9556 StartZ=0 EndX=149.963 EndY=69.6784 EndZ=0
    g55: LineSegment StartX=163.6 StartY=100.421 StartZ=0 EndX=148.6 EndY=105.881 EndZ=0
    g56: ArcOfCircle CenterX=152.124 CenterY=68.8917 CenterZ=0 NormalX=0 NormalY=0 NormalZ=1 AngleXU=2.79253 Radius=0.186667 StartAngle=4.71239 EndAngle=6.28319
    g57: LineSegment StartX=148.6 StartY=105.881 StartZ=0 EndX=148.6 EndY=106.9 EndZ=0
    g58: ArcOfCircle CenterX=152.124 CenterY=68.8917 CenterZ=0 NormalX=0 NormalY=0 NormalZ=1 AngleXU=2.79253 Radius=0.186667 StartAngle=1.5708 EndAngle=4.71239
    g59: LineSegment StartX=148.6 StartY=106.9 StartZ=0 EndX=163.338 EndY=106.9 EndZ=0
    g60: LineSegment StartX=144.12 StartY=46.9 StartZ=0 EndX=152.06 EndY=68.7163 EndZ=0
    g61: LineSegment StartX=134.122 StartY=46.9 StartZ=0 EndX=144.12 EndY=46.9 EndZ=0
    g62: ArcOfCircle CenterX=133.935 CenterY=46.9 CenterZ=0 NormalX=0 NormalY=0 NormalZ=1 AngleXU=1.5708 Radius=0.186667 StartAngle=1.5708 EndAngle=4.71239
    g63: ArcOfCircle CenterX=133.935 CenterY=46.9 CenterZ=0 NormalX=0 NormalY=0 NormalZ=1 AngleXU=1.5708 Radius=0.186667 StartAngle=0 EndAngle=1.5708
    g64: LineSegment StartX=133.935 StartY=47.0867 StartZ=0 EndX=133.935 EndY=49.2 EndZ=0
    g65: LineSegment StartX=133.635 StartY=49.5 StartZ=0 EndX=133.935 EndY=49.2 EndZ=0
    g66: LineSegment StartX=173.375 StartY=109.5 StartZ=0 EndX=173.675 EndY=109.2 EndZ=0
    g67: LineSegment StartX=173.675 StartY=107.087 StartZ=0 EndX=173.675 EndY=109.2 EndZ=0
    g68: LineSegment StartX=123.785 StartY=49.2 StartZ=0 EndX=124.085 EndY=49.5 EndZ=0
    g69: ArcOfCircle CenterX=173.675 CenterY=106.9 CenterZ=0 NormalX=0 NormalY=0 NormalZ=1 AngleXU=1.5708 Radius=0.186667 StartAngle=0 EndAngle=1.5708
    g70: LineSegment StartX=123.785 StartY=47.0867 StartZ=0 EndX=123.785 EndY=49.2 EndZ=0
    g71: ArcOfCircle CenterX=173.675 CenterY=106.9 CenterZ=0 NormalX=0 NormalY=0 NormalZ=1 AngleXU=1.5708 Radius=0.186667 StartAngle=1.5708 EndAngle=4.71239
    g72: ArcOfCircle CenterX=123.785 CenterY=46.9 CenterZ=0 NormalX=0 NormalY=0 NormalZ=1 AngleXU=1.5708 Radius=0.186667 StartAngle=4.71239 EndAngle=6.28319
    g73: LineSegment StartX=173.862 StartY=106.9 StartZ=0 EndX=188.1 EndY=106.9 EndZ=0
    g74: ArcOfCircle CenterX=123.785 CenterY=46.9 CenterZ=0 NormalX=0 NormalY=0 NormalZ=1 AngleXU=1.5708 Radius=0.186667 StartAngle=1.5708 EndAngle=4.71239
    g75: LineSegment StartX=188.1 StartY=106.9 StartZ=0 EndX=188.6 EndY=106.4 EndZ=0
    g76: LineSegment StartX=114.1 StartY=46.9 StartZ=0 EndX=123.598 EndY=46.9 EndZ=0
    g77: LineSegment StartX=188.6 StartY=106.4 StartZ=0 EndX=188.6 EndY=88.4117 EndZ=0
    g78: LineSegment StartX=113.6 StartY=46.4 StartZ=0 EndX=114.1 EndY=46.9 EndZ=0
    g79: ArcOfCircle CenterX=188.6 CenterY=88.225 CenterZ=0 NormalX=0 NormalY=0 NormalZ=1 AngleXU=-7e-16 Radius=0.186667 StartAngle=1.5708 EndAngle=4.71239
    g80: LineSegment StartX=113.6 StartY=34.6617 StartZ=0 EndX=113.6 EndY=46.4 EndZ=0
    g81: ArcOfCircle CenterX=188.6 CenterY=88.225 CenterZ=0 NormalX=0 NormalY=0 NormalZ=1 AngleXU=-7e-16 Radius=0.186667 StartAngle=4.71239 EndAngle=6.28319
    g82: ArcOfCircle CenterX=113.6 CenterY=34.475 CenterZ=0 NormalX=0 NormalY=0 NormalZ=1 AngleXU=3.14159 Radius=0.186667 StartAngle=1.5708 EndAngle=4.71239
    g83: LineSegment StartX=188.787 StartY=88.225 StartZ=0 EndX=190.9 EndY=88.225 EndZ=0
    g84: ArcOfCircle CenterX=113.6 CenterY=34.475 CenterZ=0 NormalX=0 NormalY=0 NormalZ=1 AngleXU=3.14159 Radius=0.186667 StartAngle=0 EndAngle=1.5708
    g85: LineSegment StartX=190.9 StartY=88.225 StartZ=0 EndX=191.2 EndY=87.925 EndZ=0
    g86: LineSegment StartX=113.413 StartY=34.475 StartZ=0 EndX=111.3 EndY=34.475 EndZ=0
    g87: LineSegment StartX=111 StartY=34.175 StartZ=0 EndX=111.3 EndY=34.475 EndZ=0
    g88: LineSegment StartX=191.2 StartY=78.375 StartZ=0 EndX=190.9 EndY=78.075 EndZ=0
    g89: LineSegment StartX=188.787 StartY=78.075 StartZ=0 EndX=190.9 EndY=78.075 EndZ=0
    g90: LineSegment StartX=111.3 StartY=24.325 StartZ=0 EndX=111 EndY=24.625 EndZ=0
    g91: ArcOfCircle CenterX=188.6 CenterY=78.075 CenterZ=0 NormalX=0 NormalY=0 NormalZ=1 AngleXU=-7e-16 Radius=0.186667 StartAngle=0 EndAngle=1.5708
    g92: LineSegment StartX=113.413 StartY=24.325 StartZ=0 EndX=111.3 EndY=24.325 EndZ=0
    g93: ArcOfCircle CenterX=188.6 CenterY=78.075 CenterZ=0 NormalX=0 NormalY=0 NormalZ=1 AngleXU=-7e-16 Radius=0.186667 StartAngle=1.5708 EndAngle=4.71239
    g94: ArcOfCircle CenterX=113.6 CenterY=24.325 CenterZ=0 NormalX=0 NormalY=0 NormalZ=1 AngleXU=3.14159 Radius=0.186667 StartAngle=4.71239 EndAngle=6.28319
    g95: LineSegment StartX=188.6 StartY=77.8883 StartZ=0 EndX=188.6 EndY=40.9117 EndZ=0
    g96: ArcOfCircle CenterX=113.6 CenterY=24.325 CenterZ=0 NormalX=0 NormalY=0 NormalZ=1 AngleXU=3.14159 Radius=0.186667 StartAngle=1.5708 EndAngle=4.71239
    g97: ArcOfCircle CenterX=188.6 CenterY=40.725 CenterZ=0 NormalX=0 NormalY=0 NormalZ=1 AngleXU=-7e-16 Radius=0.186667 StartAngle=1.5708 EndAngle=4.71239
    g98: LineSegment StartX=113.6 StartY=12.4 StartZ=0 EndX=113.6 EndY=24.1383 EndZ=0
    g99: ArcOfCircle CenterX=188.6 CenterY=40.725 CenterZ=0 NormalX=0 NormalY=0 NormalZ=1 AngleXU=-7e-16 Radius=0.186667 StartAngle=4.71239 EndAngle=6.28319
    g100: LineSegment StartX=114.1 StartY=11.9 StartZ=0 EndX=113.6 EndY=12.4 EndZ=0
    g101: LineSegment StartX=188.787 StartY=40.725 StartZ=0 EndX=190.9 EndY=40.725 EndZ=0
    g102: LineSegment StartX=127.088 StartY=11.9 StartZ=0 EndX=114.1 EndY=11.9 EndZ=0
    g103: LineSegment StartX=190.9 StartY=40.725 StartZ=0 EndX=191.2 EndY=40.425 EndZ=0
    g104: ArcOfCircle CenterX=127.275 CenterY=11.9 CenterZ=0 NormalX=0 NormalY=0 NormalZ=1 AngleXU=-1.5708 Radius=0.186667 StartAngle=1.5708 EndAngle=4.71239
    g105: ArcOfCircle CenterX=127.275 CenterY=11.9 CenterZ=0 NormalX=0 NormalY=0 NormalZ=1 AngleXU=-1.5708 Radius=0.186667 StartAngle=0 EndAngle=1.5708
    g106: LineSegment StartX=191.2 StartY=30.875 StartZ=0 EndX=190.9 EndY=30.575 EndZ=0
    g107: LineSegment StartX=127.275 StartY=11.7133 StartZ=0 EndX=127.275 EndY=9.6 EndZ=0
    g108: LineSegment StartX=188.787 StartY=30.575 StartZ=0 EndX=190.9 EndY=30.575 EndZ=0
    g109: LineSegment StartX=127.575 StartY=9.3 StartZ=0 EndX=127.275 EndY=9.6 EndZ=0
    g110: ArcOfCircle CenterX=188.6 CenterY=30.575 CenterZ=0 NormalX=0 NormalY=0 NormalZ=1 AngleXU=-7e-16 Radius=0.186667 StartAngle=0 EndAngle=1.5708
    g111: ArcOfCircle CenterX=188.6 CenterY=30.575 CenterZ=0 NormalX=0 NormalY=0 NormalZ=1 AngleXU=-7e-16 Radius=0.186667 StartAngle=1.5708 EndAngle=4.71239
    g112: LineSegment StartX=137.425 StartY=9.6 StartZ=0 EndX=137.125 EndY=9.3 EndZ=0
    g113: LineSegment StartX=188.6 StartY=30.3883 StartZ=0 EndX=188.6 EndY=12.4 EndZ=0
    g114: LineSegment StartX=137.425 StartY=11.7133 StartZ=0 EndX=137.425 EndY=9.6 EndZ=0
    g115: LineSegment StartX=188.6 StartY=12.4 StartZ=0 EndX=188.1 EndY=11.9 EndZ=0
    g116: ArcOfCircle CenterX=137.425 CenterY=11.9 CenterZ=0 NormalX=0 NormalY=0 NormalZ=1 AngleXU=-1.5708 Radius=0.186667 StartAngle=4.71239 EndAngle=6.28319
    g117: LineSegment StartX=188.1 StartY=11.9 StartZ=0 EndX=175.112 EndY=11.9 EndZ=0
    g118: ArcOfCircle CenterX=137.425 CenterY=11.9 CenterZ=0 NormalX=0 NormalY=0 NormalZ=1 AngleXU=-1.5708 Radius=0.186667 StartAngle=1.5708 EndAngle=4.71239
    g119: ArcOfCircle CenterX=174.925 CenterY=11.9 CenterZ=0 NormalX=0 NormalY=0 NormalZ=1 AngleXU=-1.5708 Radius=0.186667 StartAngle=1.5708 EndAngle=4.71239
    g120: LineSegment StartX=164.588 StartY=11.9 StartZ=0 EndX=137.612 EndY=11.9 EndZ=0
    g121: ArcOfCircle CenterX=174.925 CenterY=11.9 CenterZ=0 NormalX=0 NormalY=0 NormalZ=1 AngleXU=-1.5708 Radius=0.186667 StartAngle=4.71239 EndAngle=6.28319
    g122: ArcOfCircle CenterX=164.775 CenterY=11.9 CenterZ=0 NormalX=0 NormalY=0 NormalZ=1 AngleXU=-1.5708 Radius=0.186667 StartAngle=1.5708 EndAngle=4.71239
    g123: LineSegment StartX=174.925 StartY=11.7133 StartZ=0 EndX=174.925 EndY=9.6 EndZ=0
    g124: ArcOfCircle CenterX=164.775 CenterY=11.9 CenterZ=0 NormalX=0 NormalY=0 NormalZ=1 AngleXU=-1.5708 Radius=0.186667 StartAngle=0 EndAngle=1.5708
    g125: LineSegment StartX=174.925 StartY=9.6 StartZ=0 EndX=174.625 EndY=9.3 EndZ=0
    g126: LineSegment StartX=164.775 StartY=11.7133 StartZ=0 EndX=164.775 EndY=9.6 EndZ=0
    g127: LineSegment StartX=165.075 StartY=9.3 StartZ=0 EndX=164.775 EndY=9.6 EndZ=0
    g128: LineSegment StartX=159.582 StartY=62.5476 StartZ=0 EndX=161.931 EndY=61.6926 EndZ=0
    g129: ArcOfCircle CenterX=160.392 CenterY=57.464 CenterZ=0 NormalX=0 NormalY=0 NormalZ=1 AngleXU=-7e-16 Radius=4.5 StartAngle=5.93412 EndAngle=7.50492
    g130: LineSegment StartX=164.621 StartY=55.9249 StartZ=0 EndX=162.397 EndY=49.8169 EndZ=0
    g131: ArcOfCircle CenterX=158.169 CenterY=51.356 CenterZ=0 NormalX=0 NormalY=0 NormalZ=1 AngleXU=-7e-16 Radius=4.5 StartAngle=4.36332 EndAngle=5.93412
    g132: LineSegment StartX=156.63 StartY=47.1273 StartZ=0 EndX=154.28 EndY=47.9824 EndZ=0
    g133: ArcOfCircle CenterX=155.82 CenterY=52.211 CenterZ=0 NormalX=0 NormalY=0 NormalZ=1 AngleXU=-7e-16 Radius=4.5 StartAngle=2.79253 EndAngle=4.36332
    g134: LineSegment StartX=151.591 StartY=53.7501 StartZ=0 EndX=153.814 EndY=59.8581 EndZ=0
    g135: ArcOfCircle CenterX=158.043 CenterY=58.319 CenterZ=0 NormalX=0 NormalY=0 NormalZ=1 AngleXU=-7e-16 Radius=4.5 StartAngle=1.22173 EndAngle=2.79253
    g136: LineSegment StartX=183.406 StartY=81.1897 StartZ=0 EndX=184.824 EndY=80.6732 EndZ=0
    g137: LineSegment StartX=184.824 StartY=80.6732 StartZ=0 EndX=180.72 EndY=69.3969 EndZ=0
    g138: LineSegment StartX=179.301 StartY=69.9134 StartZ=0 EndX=180.72 EndY=69.3969 EndZ=0
    g139: LineSegment StartX=183.406 StartY=81.1897 StartZ=0 EndX=179.301 EndY=69.9134 EndZ=0
    g140: LineSegment StartX=172.461 StartY=51.1195 StartZ=0 EndX=173.88 EndY=50.6031 EndZ=0
    g141: LineSegment StartX=173.88 StartY=50.6031 StartZ=0 EndX=169.776 EndY=39.3268 EndZ=0
    g142: LineSegment StartX=168.357 StartY=39.8432 StartZ=0 EndX=169.776 EndY=39.3268 EndZ=0
    g143: LineSegment StartX=172.461 StartY=51.1195 StartZ=0 EndX=168.357 EndY=39.8432 EndZ=0
    g144: LineSegment StartX=121.3 StartY=42.01 StartZ=0 EndX=121.3 EndY=40.5 EndZ=0
    g145: LineSegment StartX=121.3 StartY=42.01 StartZ=0 EndX=133.3 EndY=42.01 EndZ=0
    g146: LineSegment StartX=133.3 StartY=42.01 StartZ=0 EndX=133.3 EndY=40.5 EndZ=0
    g147: LineSegment StartX=121.3 StartY=40.5 StartZ=0 EndX=133.3 EndY=40.5 EndZ=0
    g148: ArcOfCircle CenterX=169.102 CenterY=53.2467 CenterZ=0 NormalX=0 NormalY=0 NormalZ=1 AngleXU=-7e-16 Radius=2.5 StartAngle=5.93412 EndAngle=9.07571
    g149: LineSegment StartX=171.451 StartY=52.3917 StartZ=0 EndX=170.049 EndY=48.5389 EndZ=0
    g150: ArcOfCircle CenterX=167.699 CenterY=49.394 CenterZ=0 NormalX=0 NormalY=0 NormalZ=1 AngleXU=-7e-16 Radius=2.5 StartAngle=2.79253 EndAngle=5.93412
    g151: LineSegment StartX=166.752 StartY=54.1018 StartZ=0 EndX=165.35 EndY=50.249 EndZ=0
    g152: LineSegment StartX=168.876 StartY=109.5 StartZ=0 EndX=190.767 EndY=109.5 EndZ=0
    g153: LineSegment StartX=168.876 StartY=114.5 StartZ=0 EndX=193.7 EndY=114.5 EndZ=0
    g154: LineSegment StartX=169.196 StartY=9.3 StartZ=0 EndX=111.433 EndY=9.3 EndZ=0
    g155: LineSegment StartX=169.196 StartY=4.3 StartZ=0 EndX=108.5 EndY=4.3 EndZ=0
  constraints (16):
    c: PointOnObject(g45,g43)
    c: PointOnObject(g66,g152)
    c: PointOnObject(g49,g25)
    c: PointOnObject(g52,g25)
    c: PointOnObject(g65,g27)
    c: PointOnObject(g68,g27)
    c: PointOnObject(g87,g31)
    c: PointOnObject(g90,g31)
    c: PointOnObject(g109,g154)
    c: PointOnObject(g112,g154)
    c: PointOnObject(g127,g154)
    c: PointOnObject(g125,g35)
    c: PointOnObject(g106,g39)
    c: PointOnObject(g103,g39)
    c: PointOnObject(g88,g39)
    c: PointOnObject(g85,g39)
FEATURE [Sketcher::SketchObject] Sketch003
  ArcFitTolerance = 1e-06
  FullyConstrained = false
  MakeInternals = false
  sketch-geometry (144):
    g0: LineSegment StartX=57.2 StartY=114.7 StartZ=0 EndX=32.4078 EndY=114.7 EndZ=0
    g1: ArcOfCircle CenterX=57.2 CenterY=112.2 CenterZ=0 NormalX=0 NormalY=0 NormalZ=1 AngleXU=-3.14159 Radius=2.5 StartAngle=3.14159 EndAngle=4.71239
    g2: ArcOfCircle CenterX=7 CenterY=112.2 CenterZ=0 NormalX=0 NormalY=0 NormalZ=1 AngleXU=-3.14159 Radius=2.5 StartAngle=4.71239 EndAngle=6.28319
    g3: LineSegment StartX=59.7 StartY=102.831 StartZ=0 EndX=59.7 EndY=112.2 EndZ=0
    g4: LineSegment StartX=4.5 StartY=112.2 StartZ=0 EndX=4.5 EndY=7 EndZ=0
    g5: ArcOfCircle CenterX=57.2 CenterY=102.831 CenterZ=0 NormalX=0 NormalY=0 NormalZ=1 AngleXU=-3.14159 Radius=2.5 StartAngle=1.91986 EndAngle=3.14159
    g6: ArcOfCircle CenterX=7 CenterY=7 CenterZ=0 NormalX=0 NormalY=0 NormalZ=1 AngleXU=-3.14159 Radius=2.5 StartAngle=0 EndAngle=1.5708
    g7: LineSegment StartX=49.0871 StartY=97.2174 StartZ=0 EndX=58.0551 EndY=100.481 EndZ=0
    g8: LineSegment StartX=7 StartY=4.5 StartZ=0 EndX=30.0732 EndY=4.5 EndZ=0
    g9: ArcOfCircle CenterX=49.9422 CenterY=94.8682 CenterZ=0 NormalX=0 NormalY=0 NormalZ=1 AngleXU=-3.14159 Radius=2.5 StartAngle=5.06145 EndAngle=6.63225
    g10: ArcOfCircle CenterX=92.2 CenterY=7 CenterZ=0 NormalX=0 NormalY=0 NormalZ=1 AngleXU=-3.14159 Radius=2.5 StartAngle=1.5708 EndAngle=3.14159
    g11: LineSegment StartX=61.303 StartY=56.3449 StartZ=0 EndX=47.5929 EndY=94.0131 EndZ=0
    g12: LineSegment StartX=94.7 StartY=7 StartZ=0 EndX=94.7 EndY=52.2 EndZ=0
    g13: ArcOfCircle CenterX=63.6523 CenterY=57.2 CenterZ=0 NormalX=0 NormalY=0 NormalZ=1 AngleXU=-3.14159 Radius=2.5 StartAngle=0.349066 EndAngle=1.5708
    g14: ArcOfCircle CenterX=92.2 CenterY=52.2 CenterZ=0 NormalX=0 NormalY=0 NormalZ=1 AngleXU=-3.14159 Radius=2.5 StartAngle=3.14159 EndAngle=4.71239
    g15: LineSegment StartX=92.2 StartY=54.7 StartZ=0 EndX=63.6523 EndY=54.7 EndZ=0
    g16: ArcOfCircle CenterX=54.267 CenterY=109.95 CenterZ=0 NormalX=0 NormalY=0 NormalZ=1 AngleXU=-3.14159 Radius=0.25 StartAngle=1.5708 EndAngle=2.61799
    g17: ArcOfCircle CenterX=54.7 CenterY=109.7 CenterZ=0 NormalX=0 NormalY=0 NormalZ=1 AngleXU=-3.14159 Radius=0.25 StartAngle=2.0944 EndAngle=5.75959
    g18: ArcOfCircle CenterX=54.95 CenterY=109.267 CenterZ=0 NormalX=0 NormalY=0 NormalZ=1 AngleXU=-3.14159 Radius=0.25 StartAngle=5.23599 EndAngle=6.28319
    g19: LineSegment StartX=54.7 StartY=104.693 StartZ=0 EndX=54.7 EndY=109.267 EndZ=0
    g20: ArcOfCircle CenterX=54.95 CenterY=104.693 CenterZ=0 NormalX=0 NormalY=0 NormalZ=1 AngleXU=-3.14159 Radius=0.25 StartAngle=0 EndAngle=1.0472
    g21: ArcOfCircle CenterX=54.7 CenterY=104.26 CenterZ=0 NormalX=0 NormalY=0 NormalZ=1 AngleXU=-3.14159 Radius=0.25 StartAngle=0.872665 EndAngle=4.18879
    g22: ArcOfCircle CenterX=54.3786 CenterY=103.877 CenterZ=0 NormalX=0 NormalY=0 NormalZ=1 AngleXU=-3.14159 Radius=0.25 StartAngle=4.01426 EndAngle=5.06145
    g23: LineSegment StartX=41.3721 StartY=99.4094 StartZ=0 EndX=54.2931 EndY=104.112 EndZ=0
    g24: ArcOfCircle CenterX=41.7142 CenterY=98.4697 CenterZ=0 NormalX=0 NormalY=0 NormalZ=1 AngleXU=-3.14159 Radius=1 StartAngle=5.06145 EndAngle=6.63225
    g25: LineSegment StartX=58.1612 StartY=50.358 StartZ=0 EndX=40.7745 EndY=98.1277 EndZ=0
    g26: ArcOfCircle CenterX=59.1009 CenterY=50.7 CenterZ=0 NormalX=0 NormalY=0 NormalZ=1 AngleXU=-3.14159 Radius=1 StartAngle=0.349066 EndAngle=1.5708
    g27: LineSegment StartX=89.267 StartY=49.7 StartZ=0 EndX=59.1009 EndY=49.7 EndZ=0
    g28: ArcOfCircle CenterX=89.267 CenterY=49.95 CenterZ=0 NormalX=0 NormalY=0 NormalZ=1 AngleXU=-3.14159 Radius=0.25 StartAngle=1.5708 EndAngle=2.61799
    g29: ArcOfCircle CenterX=89.7 CenterY=49.7 CenterZ=0 NormalX=0 NormalY=0 NormalZ=1 AngleXU=-3.14159 Radius=0.25 StartAngle=2.0944 EndAngle=5.75959
    g30: ArcOfCircle CenterX=89.95 CenterY=49.267 CenterZ=0 NormalX=0 NormalY=0 NormalZ=1 AngleXU=-3.14159 Radius=0.25 StartAngle=5.23599 EndAngle=6.28319
    g31: LineSegment StartX=89.7 StartY=9.93301 StartZ=0 EndX=89.7 EndY=49.267 EndZ=0
    g32: ArcOfCircle CenterX=89.95 CenterY=9.93301 CenterZ=0 NormalX=0 NormalY=0 NormalZ=1 AngleXU=-3.14159 Radius=0.25 StartAngle=0 EndAngle=1.0472
    g33: ArcOfCircle CenterX=89.7 CenterY=9.5 CenterZ=0 NormalX=0 NormalY=0 NormalZ=1 AngleXU=-3.14159 Radius=0.25 StartAngle=0.523599 EndAngle=4.18879
    g34: ArcOfCircle CenterX=89.267 CenterY=9.25 CenterZ=0 NormalX=0 NormalY=0 NormalZ=1 AngleXU=-3.14159 Radius=0.25 StartAngle=3.66519 EndAngle=4.71239
    g35: LineSegment StartX=9.93301 StartY=9.5 StartZ=0 EndX=30.0732 EndY=9.5 EndZ=0
    g36: ArcOfCircle CenterX=9.93301 CenterY=9.25 CenterZ=0 NormalX=0 NormalY=0 NormalZ=1 AngleXU=-3.14159 Radius=0.25 StartAngle=4.71239 EndAngle=5.75959
    g37: ArcOfCircle CenterX=9.5 CenterY=9.5 CenterZ=0 NormalX=0 NormalY=0 NormalZ=1 AngleXU=-3.14159 Radius=0.25 StartAngle=5.23599 EndAngle=8.90118
    g38: ArcOfCircle CenterX=9.25 CenterY=9.93301 CenterZ=0 NormalX=0 NormalY=0 NormalZ=1 AngleXU=-3.14159 Radius=0.25 StartAngle=2.0944 EndAngle=3.14159
    g39: LineSegment StartX=9.5 StartY=109.267 StartZ=0 EndX=9.5 EndY=9.93301 EndZ=0
    g40: ArcOfCircle CenterX=9.25 CenterY=109.267 CenterZ=0 NormalX=0 NormalY=0 NormalZ=1 AngleXU=-3.14159 Radius=0.25 StartAngle=3.14159 EndAngle=4.18879
    g41: ArcOfCircle CenterX=9.5 CenterY=109.7 CenterZ=0 NormalX=0 NormalY=0 NormalZ=1 AngleXU=-3.14159 Radius=0.25 StartAngle=3.66519 EndAngle=7.33038
    g42: ArcOfCircle CenterX=9.93301 CenterY=109.95 CenterZ=0 NormalX=0 NormalY=0 NormalZ=1 AngleXU=-3.14159 Radius=0.25 StartAngle=0.523599 EndAngle=1.5708
    g43: LineSegment StartX=54.267 StartY=109.7 StartZ=0 EndX=32.4078 EndY=109.7 EndZ=0
    g44: LineSegment StartX=37.075 StartY=107.287 StartZ=0 EndX=37.075 EndY=109.4 EndZ=0
    g45: LineSegment StartX=37.075 StartY=109.4 StartZ=0 EndX=36.775 EndY=109.7 EndZ=0
    g46: ArcOfCircle CenterX=37.075 CenterY=107.1 CenterZ=0 NormalX=0 NormalY=0 NormalZ=1 AngleXU=1.5708 Radius=0.186667 StartAngle=0 EndAngle=1.5708
    g47: ArcOfCircle CenterX=37.075 CenterY=107.1 CenterZ=0 NormalX=0 NormalY=0 NormalZ=1 AngleXU=1.5708 Radius=0.186667 StartAngle=1.5708 EndAngle=4.71239
    g48: LineSegment StartX=27.225 StartY=109.7 StartZ=0 EndX=26.925 EndY=109.4 EndZ=0
    g49: LineSegment StartX=52 StartY=107.1 StartZ=0 EndX=37.2617 EndY=107.1 EndZ=0
    g50: LineSegment StartX=26.925 StartY=107.287 StartZ=0 EndX=26.925 EndY=109.4 EndZ=0
    g51: LineSegment StartX=52 StartY=106.081 StartZ=0 EndX=52 EndY=107.1 EndZ=0
    g52: ArcOfCircle CenterX=26.925 CenterY=107.1 CenterZ=0 NormalX=0 NormalY=0 NormalZ=1 AngleXU=1.5708 Radius=0.186667 StartAngle=4.71239 EndAngle=6.28319
    g53: LineSegment StartX=37 StartY=100.621 StartZ=0 EndX=52 EndY=106.081 EndZ=0
    g54: ArcOfCircle CenterX=26.925 CenterY=107.1 CenterZ=0 NormalX=0 NormalY=0 NormalZ=1 AngleXU=1.5708 Radius=0.186667 StartAngle=1.5708 EndAngle=4.71239
    g55: LineSegment StartX=44.9405 StartY=78.805 StartZ=0 EndX=37 EndY=100.621 EndZ=0
    g56: LineSegment StartX=26.7383 StartY=107.1 StartZ=0 EndX=12.5 EndY=107.1 EndZ=0
    g57: ArcOfCircle CenterX=45.0043 CenterY=78.6296 CenterZ=0 NormalX=0 NormalY=0 NormalZ=1 AngleXU=0.349066 Radius=0.186667 StartAngle=1.5708 EndAngle=4.71239
    g58: LineSegment StartX=12.5 StartY=107.1 StartZ=0 EndX=12 EndY=106.6 EndZ=0
    g59: ArcOfCircle CenterX=45.0043 CenterY=78.6296 CenterZ=0 NormalX=0 NormalY=0 NormalZ=1 AngleXU=0.349066 Radius=0.186667 StartAngle=4.71239 EndAngle=6.28319
    g60: LineSegment StartX=12 StartY=106.6 StartZ=0 EndX=12 EndY=88.6117 EndZ=0
    g61: LineSegment StartX=45.1797 StartY=78.6934 StartZ=0 EndX=47.1656 EndY=79.4163 EndZ=0
    g62: ArcOfCircle CenterX=12 CenterY=88.425 CenterZ=0 NormalX=0 NormalY=0 NormalZ=1 AngleXU=-3.14159 Radius=0.186667 StartAngle=1.5708 EndAngle=4.71239
    g63: LineSegment StartX=47.6706 StartY=79.1808 StartZ=0 EndX=47.1656 EndY=79.4163 EndZ=0
    g64: ArcOfCircle CenterX=12 CenterY=88.425 CenterZ=0 NormalX=0 NormalY=0 NormalZ=1 AngleXU=-3.14159 Radius=0.186667 StartAngle=0 EndAngle=1.5708
    g65: LineSegment StartX=11.8133 StartY=88.425 StartZ=0 EndX=9.7 EndY=88.425 EndZ=0
    g66: LineSegment StartX=50.6371 StartY=69.8784 StartZ=0 EndX=50.8726 EndY=70.3833 EndZ=0
    g67: LineSegment StartX=9.7 StartY=88.425 StartZ=0 EndX=9.5 EndY=88.225 EndZ=0
    g68: LineSegment StartX=48.6512 StartY=69.1556 StartZ=0 EndX=50.6371 EndY=69.8784 EndZ=0
    g69: ArcOfCircle CenterX=48.4758 CenterY=69.0917 CenterZ=0 NormalX=0 NormalY=0 NormalZ=1 AngleXU=0.349066 Radius=0.186667 StartAngle=0 EndAngle=1.5708
    g70: LineSegment StartX=9.5 StartY=78.475 StartZ=0 EndX=9.7 EndY=78.275 EndZ=0
    g71: ArcOfCircle CenterX=48.4758 CenterY=69.0917 CenterZ=0 NormalX=0 NormalY=0 NormalZ=1 AngleXU=0.349066 Radius=0.186667 StartAngle=1.5708 EndAngle=4.71239
    g72: LineSegment StartX=11.8133 StartY=78.275 StartZ=0 EndX=9.7 EndY=78.275 EndZ=0
    g73: LineSegment StartX=56.4802 StartY=47.1 StartZ=0 EndX=48.5397 EndY=68.9163 EndZ=0
    g74: ArcOfCircle CenterX=12 CenterY=78.275 CenterZ=0 NormalX=0 NormalY=0 NormalZ=1 AngleXU=-3.14159 Radius=0.186667 StartAngle=4.71239 EndAngle=6.28319
    g75: LineSegment StartX=66.4784 StartY=47.1 StartZ=0 EndX=56.4802 EndY=47.1 EndZ=0
    g76: ArcOfCircle CenterX=12 CenterY=78.275 CenterZ=0 NormalX=0 NormalY=0 NormalZ=1 AngleXU=-3.14159 Radius=0.186667 StartAngle=1.5708 EndAngle=4.71239
    g77: ArcOfCircle CenterX=66.6651 CenterY=47.1 CenterZ=0 NormalX=0 NormalY=0 NormalZ=1 AngleXU=1.5708 Radius=0.186667 StartAngle=1.5708 EndAngle=4.71239
    g78: LineSegment StartX=12 StartY=78.0883 StartZ=0 EndX=12 EndY=41.1117 EndZ=0
    g79: ArcOfCircle CenterX=66.6651 CenterY=47.1 CenterZ=0 NormalX=0 NormalY=0 NormalZ=1 AngleXU=1.5708 Radius=0.186667 StartAngle=4.71239 EndAngle=6.28319
    g80: ArcOfCircle CenterX=12 CenterY=40.925 CenterZ=0 NormalX=0 NormalY=0 NormalZ=1 AngleXU=-3.14159 Radius=0.186667 StartAngle=1.5708 EndAngle=4.71239
    g81: LineSegment StartX=66.6651 StartY=47.2867 StartZ=0 EndX=66.6651 EndY=49.4 EndZ=0
    g82: ArcOfCircle CenterX=12 CenterY=40.925 CenterZ=0 NormalX=0 NormalY=0 NormalZ=1 AngleXU=-3.14159 Radius=0.186667 StartAngle=0 EndAngle=1.5708
    g83: LineSegment StartX=66.9651 StartY=49.7 StartZ=0 EndX=66.6651 EndY=49.4 EndZ=0
    g84: LineSegment StartX=11.8133 StartY=40.925 StartZ=0 EndX=9.7 EndY=40.925 EndZ=0
    g85: LineSegment StartX=9.7 StartY=40.925 StartZ=0 EndX=9.5 EndY=40.725 EndZ=0
    g86: LineSegment StartX=76.8151 StartY=49.4 StartZ=0 EndX=76.5151 EndY=49.7 EndZ=0
    g87: LineSegment StartX=76.8151 StartY=47.2867 StartZ=0 EndX=76.8151 EndY=49.4 EndZ=0
    g88: LineSegment StartX=9.5 StartY=30.975 StartZ=0 EndX=9.7 EndY=30.775 EndZ=0
    g89: ArcOfCircle CenterX=76.8151 CenterY=47.1 CenterZ=0 NormalX=0 NormalY=0 NormalZ=1 AngleXU=1.5708 Radius=0.186667 StartAngle=0 EndAngle=1.5708
    g90: LineSegment StartX=11.8133 StartY=30.775 StartZ=0 EndX=9.7 EndY=30.775 EndZ=0
    g91: ArcOfCircle CenterX=76.8151 CenterY=47.1 CenterZ=0 NormalX=0 NormalY=0 NormalZ=1 AngleXU=1.5708 Radius=0.186667 StartAngle=1.5708 EndAngle=4.71239
    g92: ArcOfCircle CenterX=12 CenterY=30.775 CenterZ=0 NormalX=0 NormalY=0 NormalZ=1 AngleXU=-3.14159 Radius=0.186667 StartAngle=4.71239 EndAngle=6.28319
    g93: LineSegment StartX=86.5 StartY=47.1 StartZ=0 EndX=77.0018 EndY=47.1 EndZ=0
    g94: ArcOfCircle CenterX=12 CenterY=30.775 CenterZ=0 NormalX=0 NormalY=0 NormalZ=1 AngleXU=-3.14159 Radius=0.186667 StartAngle=1.5708 EndAngle=4.71239
    g95: LineSegment StartX=87 StartY=46.6 StartZ=0 EndX=86.5 EndY=47.1 EndZ=0
    g96: LineSegment StartX=12 StartY=30.5883 StartZ=0 EndX=12 EndY=12.6 EndZ=0
    g97: LineSegment StartX=87 StartY=34.8617 StartZ=0 EndX=87 EndY=46.6 EndZ=0
    g98: LineSegment StartX=12 StartY=12.6 StartZ=0 EndX=12.5 EndY=12.1 EndZ=0
    g99: ArcOfCircle CenterX=87 CenterY=34.675 CenterZ=0 NormalX=0 NormalY=0 NormalZ=1 AngleXU=2e-16 Radius=0.186667 StartAngle=1.5708 EndAngle=4.71239
    g100: LineSegment StartX=12.5 StartY=12.1 StartZ=0 EndX=25.4883 EndY=12.1 EndZ=0
    g101: ArcOfCircle CenterX=87 CenterY=34.675 CenterZ=0 NormalX=0 NormalY=0 NormalZ=1 AngleXU=2e-16 Radius=0.186667 StartAngle=4.71239 EndAngle=6.28319
    g102: ArcOfCircle CenterX=25.675 CenterY=12.1 CenterZ=0 NormalX=0 NormalY=0 NormalZ=1 AngleXU=-1.5708 Radius=0.186667 StartAngle=1.5708 EndAngle=4.71239
    g103: LineSegment StartX=87.1867 StartY=34.675 StartZ=0 EndX=89.3 EndY=34.675 EndZ=0
    g104: ArcOfCircle CenterX=25.675 CenterY=12.1 CenterZ=0 NormalX=0 NormalY=0 NormalZ=1 AngleXU=-1.5708 Radius=0.186667 StartAngle=0 EndAngle=1.5708
    g105: LineSegment StartX=89.7 StartY=34.275 StartZ=0 EndX=89.3 EndY=34.675 EndZ=0
    g106: LineSegment StartX=25.675 StartY=11.9133 StartZ=0 EndX=25.675 EndY=9.8 EndZ=0
    g107: LineSegment StartX=25.675 StartY=9.8 StartZ=0 EndX=25.975 EndY=9.5 EndZ=0
    g108: LineSegment StartX=89.3 StartY=24.525 StartZ=0 EndX=89.7 EndY=24.925 EndZ=0
    g109: LineSegment StartX=87.1867 StartY=24.525 StartZ=0 EndX=89.3 EndY=24.525 EndZ=0
    g110: LineSegment StartX=35.525 StartY=9.5 StartZ=0 EndX=35.825 EndY=9.8 EndZ=0
    g111: ArcOfCircle CenterX=87 CenterY=24.525 CenterZ=0 NormalX=0 NormalY=0 NormalZ=1 AngleXU=2e-16 Radius=0.186667 StartAngle=0 EndAngle=1.5708
    g112: LineSegment StartX=35.825 StartY=11.9133 StartZ=0 EndX=35.825 EndY=9.8 EndZ=0
    g113: ArcOfCircle CenterX=87 CenterY=24.525 CenterZ=0 NormalX=0 NormalY=0 NormalZ=1 AngleXU=2e-16 Radius=0.186667 StartAngle=1.5708 EndAngle=4.71239
    g114: ArcOfCircle CenterX=35.825 CenterY=12.1 CenterZ=0 NormalX=0 NormalY=0 NormalZ=1 AngleXU=-1.5708 Radius=0.186667 StartAngle=4.71239 EndAngle=6.28319
    g115: LineSegment StartX=87 StartY=12.6 StartZ=0 EndX=87 EndY=24.3383 EndZ=0
    g116: ArcOfCircle CenterX=35.825 CenterY=12.1 CenterZ=0 NormalX=0 NormalY=0 NormalZ=1 AngleXU=-1.5708 Radius=0.186667 StartAngle=1.5708 EndAngle=4.71239
    g117: LineSegment StartX=86.5 StartY=12.1 StartZ=0 EndX=87 EndY=12.6 EndZ=0
    g118: LineSegment StartX=36.0117 StartY=12.1 StartZ=0 EndX=62.9883 EndY=12.1 EndZ=0
    g119: LineSegment StartX=73.5117 StartY=12.1 StartZ=0 EndX=86.5 EndY=12.1 EndZ=0
    g120: ArcOfCircle CenterX=63.175 CenterY=12.1 CenterZ=0 NormalX=0 NormalY=0 NormalZ=1 AngleXU=-1.5708 Radius=0.186667 StartAngle=1.5708 EndAngle=4.71239
    g121: ArcOfCircle CenterX=73.325 CenterY=12.1 CenterZ=0 NormalX=0 NormalY=0 NormalZ=1 AngleXU=-1.5708 Radius=0.186667 StartAngle=1.5708 EndAngle=4.71239
    g122: ArcOfCircle CenterX=63.175 CenterY=12.1 CenterZ=0 NormalX=0 NormalY=0 NormalZ=1 AngleXU=-1.5708 Radius=0.186667 StartAngle=0 EndAngle=1.5708
    g123: ArcOfCircle CenterX=73.325 CenterY=12.1 CenterZ=0 NormalX=0 NormalY=0 NormalZ=1 AngleXU=-1.5708 Radius=0.186667 StartAngle=4.71239 EndAngle=6.28319
    g124: LineSegment StartX=63.175 StartY=11.9133 StartZ=0 EndX=63.175 EndY=9.8 EndZ=0
    g125: LineSegment StartX=73.325 StartY=11.9133 StartZ=0 EndX=73.325 EndY=9.8 EndZ=0
    g126: LineSegment StartX=63.175 StartY=9.8 StartZ=0 EndX=63.475 EndY=9.5 EndZ=0
    g127: LineSegment StartX=73.025 StartY=9.5 StartZ=0 EndX=73.325 EndY=9.8 EndZ=0
    g128: LineSegment StartX=17.1945 StartY=81.3897 StartZ=0 EndX=15.7756 EndY=80.8732 EndZ=0
    g129: LineSegment StartX=17.1945 StartY=81.3897 StartZ=0 EndX=21.2987 EndY=70.1134 EndZ=0
    g130: LineSegment StartX=21.2987 StartY=70.1134 StartZ=0 EndX=19.8798 EndY=69.5969 EndZ=0
    g131: LineSegment StartX=15.7756 StartY=80.8732 StartZ=0 EndX=19.8798 EndY=69.5969 EndZ=0
    g132: LineSegment StartX=28.1391 StartY=51.3195 StartZ=0 EndX=26.7202 EndY=50.8031 EndZ=0
    g133: LineSegment StartX=28.1391 StartY=51.3195 StartZ=0 EndX=32.2434 EndY=40.0432 EndZ=0
    g134: LineSegment StartX=32.2434 StartY=40.0432 StartZ=0 EndX=30.8244 EndY=39.5268 EndZ=0
    g135: LineSegment StartX=26.7202 StartY=50.8031 StartZ=0 EndX=30.8244 EndY=39.5268 EndZ=0
    g136: LineSegment StartX=67.3 StartY=42.21 StartZ=0 EndX=67.3 EndY=40.7 EndZ=0
    g137: LineSegment StartX=67.3 StartY=42.21 StartZ=0 EndX=79.3 EndY=42.21 EndZ=0
    g138: LineSegment StartX=79.3 StartY=42.21 StartZ=0 EndX=79.3 EndY=40.7 EndZ=0
    g139: LineSegment StartX=67.3 StartY=40.7 StartZ=0 EndX=79.3 EndY=40.7 EndZ=0
    g140: LineSegment StartX=31.4078 StartY=114.7 StartZ=0 EndX=7 EndY=114.7 EndZ=0
    g141: LineSegment StartX=31.4078 StartY=109.7 StartZ=0 EndX=9.93301 EndY=109.7 EndZ=0
    g142: LineSegment StartX=31.0732 StartY=9.5 StartZ=0 EndX=89.267 EndY=9.5 EndZ=0
    g143: LineSegment StartX=31.0732 StartY=4.5 StartZ=0 EndX=92.2 EndY=4.5 EndZ=0
  constraints (16):
    c: PointOnObject(g45,g43)
    c: PointOnObject(g48,g141)
    c: PointOnObject(g63,g25)
    c: PointOnObject(g66,g25)
    c: PointOnObject(g83,g27)
    c: PointOnObject(g86,g27)
    c: PointOnObject(g105,g31)
    c: PointOnObject(g108,g31)
    c: PointOnObject(g127,g142)
    c: PointOnObject(g126,g142)
    c: PointOnObject(g110,g142)
    c: PointOnObject(g107,g35)
    c: PointOnObject(g88,g39)
    c: PointOnObject(g85,g39)
    c: PointOnObject(g70,g39)
    c: PointOnObject(g67,g39)
FEATURE [App::DocumentObjectGroup] Group001  label="Text"
  Group = -> [ShapeString010,ShapeString009,ShapeString008,ShapeString007,ShapeString005,ShapeString004,ShapeString003,ShapeString002,ShapeString001,ShapeString,ShapeString006]
FEATURE [Sketcher::SketchObject] Sketch004
  ArcFitTolerance = 1e-06
  FullyConstrained = false
  MakeInternals = false
  sketch-geometry (68):
    g0: LineSegment StartX=12.5 StartY=134.025 StartZ=0 EndX=14.5913 EndY=134.025 EndZ=0
    g1: LineSegment StartX=12.5 StartY=134.025 StartZ=0 EndX=12 EndY=133.525 EndZ=0
    g2: ArcOfCircle CenterX=14.7648 CenterY=134.125 CenterZ=0 NormalX=0 NormalY=0 NormalZ=1 AngleXU=-1e-16 Radius=0.200333 StartAngle=0 EndAngle=1.0472
    g3: ArcOfCircle CenterX=14.7648 CenterY=134.125 CenterZ=0 NormalX=0 NormalY=0 NormalZ=1 AngleXU=-1e-16 Radius=0.200333 StartAngle=3.66519 EndAngle=6.28319
    g4: LineSegment StartX=12 StartY=144.475 StartZ=0 EndX=12.5 EndY=143.975 EndZ=0
    g5: ArcOfCircle CenterX=12.4 CenterY=157.8 CenterZ=0 NormalX=0 NormalY=0 NormalZ=1 AngleXU=1.5708 Radius=0.4 StartAngle=0 EndAngle=1.5708
    g6: LineSegment StartX=12.5 StartY=143.975 StartZ=0 EndX=14.5913 EndY=143.975 EndZ=0
    g7: LineSegment StartX=26 StartY=158.2 StartZ=0 EndX=12.4 EndY=158.2 EndZ=0
    g8: ArcOfCircle CenterX=14.7648 CenterY=143.875 CenterZ=0 NormalX=0 NormalY=0 NormalZ=1 AngleXU=-1e-16 Radius=0.200333 StartAngle=0 EndAngle=2.61799
    g9: ArcOfCircle CenterX=26 CenterY=158.6 CenterZ=0 NormalX=0 NormalY=0 NormalZ=1 AngleXU=-1e-16 Radius=0.4 StartAngle=4.71239 EndAngle=7.85398
    g10: ArcOfCircle CenterX=14.7648 CenterY=143.875 CenterZ=0 NormalX=0 NormalY=0 NormalZ=1 AngleXU=-1e-16 Radius=0.200333 StartAngle=5.23599 EndAngle=6.28319
    g11: LineSegment StartX=12.4 StartY=159 StartZ=0 EndX=26 EndY=159 EndZ=0
    g12: LineSegment StartX=14.865 StartY=134.299 StartZ=0 EndX=14.865 EndY=138.512 EndZ=0
    g13: ArcOfCircle CenterX=12.4 CenterY=159.4 CenterZ=0 NormalX=0 NormalY=0 NormalZ=1 AngleXU=1.5708 Radius=0.4 StartAngle=1.5708 EndAngle=3.14159
    g14: LineSegment StartX=12 StartY=159.4 StartZ=0 EndX=12 EndY=161.553 EndZ=0
    g15: ArcOfCircle CenterX=12.4 CenterY=161.553 CenterZ=0 NormalX=0 NormalY=0 NormalZ=1 AngleXU=1.5708 Radius=0.4 StartAngle=0.463648 EndAngle=1.5708
    g16: LineSegment StartX=12.2211 StartY=161.911 StartZ=0 EndX=14 EndY=162.8 EndZ=0
    g17: LineSegment StartX=14 StartY=162.8 StartZ=0 EndX=14 EndY=161.8 EndZ=0
    g18: LineSegment StartX=12 StartY=133.525 StartZ=0 EndX=12 EndY=119.5 EndZ=0
    g19: LineSegment StartX=14 StartY=161.8 StartZ=0 EndX=16.8 EndY=161.8 EndZ=0
    g20: LineSegment StartX=12 StartY=119.5 StartZ=0 EndX=12.5 EndY=119 EndZ=0
    g21: LineSegment StartX=16.8 StartY=163.8 StartZ=0 EndX=16.8 EndY=161.8 EndZ=0
    g22: LineSegment StartX=44.5383 StartY=119 StartZ=0 EndX=12.5 EndY=119 EndZ=0
    g23: LineSegment StartX=24.2132 StartY=161.814 StartZ=0 EndX=16.8 EndY=163.8 EndZ=0
    g24: ArcOfCircle CenterX=44.725 CenterY=119 CenterZ=0 NormalX=0 NormalY=0 NormalZ=1 AngleXU=-1.5708 Radius=0.186667 StartAngle=1.5708 EndAngle=4.71239
    g25: ArcOfCircle CenterX=24.3168 CenterY=162.2 CenterZ=0 NormalX=0 NormalY=0 NormalZ=1 AngleXU=1.5708 Radius=0.4 StartAngle=2.87979 EndAngle=3.14159
    g26: ArcOfCircle CenterX=44.725 CenterY=119 CenterZ=0 NormalX=0 NormalY=0 NormalZ=1 AngleXU=-1.5708 Radius=0.186667 StartAngle=0 EndAngle=1.5708
    g27: LineSegment StartX=75.2832 StartY=161.8 StartZ=0 EndX=24.3168 EndY=161.8 EndZ=0
    g28: LineSegment StartX=44.725 StartY=118.813 StartZ=0 EndX=44.725 EndY=116.7 EndZ=0
    g29: ArcOfCircle CenterX=75.2832 CenterY=162.2 CenterZ=0 NormalX=0 NormalY=0 NormalZ=1 AngleXU=1.5708 Radius=0.4 StartAngle=3.14159 EndAngle=3.40339
    g30: LineSegment StartX=44.725 StartY=116.7 StartZ=0 EndX=45.225 EndY=116.2 EndZ=0
    g31: LineSegment StartX=82.8 StartY=163.8 StartZ=0 EndX=75.3868 EndY=161.814 EndZ=0
    g32: LineSegment StartX=45.225 StartY=116.2 StartZ=0 EndX=54.375 EndY=116.2 EndZ=0
    g33: LineSegment StartX=82.8 StartY=161.8 StartZ=0 EndX=82.8 EndY=163.8 EndZ=0
    g34: LineSegment StartX=54.375 StartY=116.2 StartZ=0 EndX=54.875 EndY=116.7 EndZ=0
    g35: LineSegment StartX=85.6 StartY=161.8 StartZ=0 EndX=82.8 EndY=161.8 EndZ=0
    g36: LineSegment StartX=54.875 StartY=118.813 StartZ=0 EndX=54.875 EndY=116.7 EndZ=0
    g37: LineSegment StartX=85.6 StartY=162.8 StartZ=0 EndX=85.6 EndY=161.8 EndZ=0
    g38: ArcOfCircle CenterX=54.875 CenterY=119 CenterZ=0 NormalX=0 NormalY=0 NormalZ=1 AngleXU=-1.5708 Radius=0.186667 StartAngle=4.71239 EndAngle=6.28319
    g39: LineSegment StartX=87.3789 StartY=161.911 StartZ=0 EndX=85.6 EndY=162.8 EndZ=0
    g40: ArcOfCircle CenterX=54.875 CenterY=119 CenterZ=0 NormalX=0 NormalY=0 NormalZ=1 AngleXU=-1.5708 Radius=0.186667 StartAngle=1.5708 EndAngle=4.71239
    g41: ArcOfCircle CenterX=87.2 CenterY=161.553 CenterZ=0 NormalX=0 NormalY=0 NormalZ=1 AngleXU=1.5708 Radius=0.4 StartAngle=4.71239 EndAngle=5.81954
    g42: LineSegment StartX=87.1 StartY=119 StartZ=0 EndX=55.0617 EndY=119 EndZ=0
    g43: LineSegment StartX=87.6 StartY=161.553 StartZ=0 EndX=87.6 EndY=159.4 EndZ=0
    g44: LineSegment StartX=87.1 StartY=119 StartZ=0 EndX=87.6 EndY=119.5 EndZ=0
    g45: ArcOfCircle CenterX=87.2 CenterY=159.4 CenterZ=0 NormalX=0 NormalY=0 NormalZ=1 AngleXU=1.5708 Radius=0.4 StartAngle=3.14159 EndAngle=4.71239
    g46: LineSegment StartX=87.6 StartY=133.525 StartZ=0 EndX=87.6 EndY=119.5 EndZ=0
    g47: LineSegment StartX=87.2 StartY=159 StartZ=0 EndX=73.6 EndY=159 EndZ=0
    g48: LineSegment StartX=87.6 StartY=133.525 StartZ=0 EndX=87.1 EndY=134.025 EndZ=0
    g49: ArcOfCircle CenterX=73.6 CenterY=158.6 CenterZ=0 NormalX=0 NormalY=0 NormalZ=1 AngleXU=-1e-16 Radius=0.4 StartAngle=1.5708 EndAngle=4.71239
    g50: LineSegment StartX=85.0087 StartY=134.025 StartZ=0 EndX=87.1 EndY=134.025 EndZ=0
    g51: LineSegment StartX=73.6 StartY=158.2 StartZ=0 EndX=87.2 EndY=158.2 EndZ=0
    g52: ArcOfCircle CenterX=84.8352 CenterY=134.125 CenterZ=0 NormalX=0 NormalY=0 NormalZ=1 AngleXU=-1e-16 Radius=0.200333 StartAngle=2.0944 EndAngle=5.75959
    g53: ArcOfCircle CenterX=87.2 CenterY=157.8 CenterZ=0 NormalX=0 NormalY=0 NormalZ=1 AngleXU=1.5708 Radius=0.4 StartAngle=4.71239 EndAngle=6.28319
    g54: LineSegment StartX=84.735 StartY=134.299 StartZ=0 EndX=84.735 EndY=138.512 EndZ=0
    g55: ArcOfCircle CenterX=84.8352 CenterY=143.875 CenterZ=0 NormalX=0 NormalY=0 NormalZ=1 AngleXU=-1e-16 Radius=0.200333 StartAngle=0.523599 EndAngle=4.18879
    g56: LineSegment StartX=87.1 StartY=143.975 StartZ=0 EndX=87.6 EndY=144.475 EndZ=0
    g57: LineSegment StartX=85.0087 StartY=143.975 StartZ=0 EndX=87.1 EndY=143.975 EndZ=0
    g58: LineSegment StartX=14.865 StartY=139.512 StartZ=0 EndX=14.865 EndY=143.701 EndZ=0
    g59: LineSegment StartX=84.735 StartY=139.512 StartZ=0 EndX=84.735 EndY=143.701 EndZ=0
    g60: LineSegment StartX=14.865 StartY=139.512 StartZ=0 EndX=14.865 EndY=138.512 EndZ=0
    g61: LineSegment StartX=84.735 StartY=138.512 StartZ=0 EndX=84.735 EndY=139.512 EndZ=0
    g62: LineSegment StartX=12 StartY=157.8 StartZ=0 EndX=12 EndY=145.804 EndZ=0
    g63: LineSegment StartX=12 StartY=144.475 StartZ=0 EndX=12 EndY=144.808 EndZ=0
    g64: LineSegment StartX=87.6 StartY=157.8 StartZ=0 EndX=87.6 EndY=145.798 EndZ=0
    g65: LineSegment StartX=87.6 StartY=144.799 StartZ=0 EndX=87.6 EndY=144.475 EndZ=0
    g66: LineSegment StartX=12 StartY=159.4 StartZ=0 EndX=12 EndY=157.8 EndZ=0
    g67: LineSegment StartX=87.6 StartY=159.4 StartZ=0 EndX=87.6 EndY=157.8 EndZ=0
  constraints (19):
    c: Coincident(g60,g58)
    c: Coincident(g60,g12)
    c: Vertical(g60)
    c: Coincident(g61,g54)
    c: Coincident(g61,g59)
    c: Vertical(g61)
    c: Tangent(g62,g5) = -1.5708
    c: Vertical(g62)
    c: Coincident(g63,g4)
    c: Vertical(g63)
    c: Tangent(g64,g53) = 1.5708
    c: Vertical(g64)
    c: Coincident(g65,g56)
    c: Vertical(g65)
    c: Coincident(g13,g66)
    c: Coincident(g43,g67)
    c: Coincident(g67,g53)
    c: Vertical(g67)
    c: Tangent(g67,g45)
FEATURE [Sketcher::SketchObject] Sketch005
  ArcFitTolerance = 1e-06
  FullyConstrained = false
  MakeInternals = false
  sketch-geometry (72):
    g0: LineSegment StartX=87.1 StartY=258 StartZ=0 EndX=12.5 EndY=258 EndZ=0
    g1: LineSegment StartX=87.1 StartY=258 StartZ=0 EndX=87.6 EndY=258.5 EndZ=0
    g2: LineSegment StartX=12.5 StartY=258 StartZ=0 EndX=12 EndY=258.5 EndZ=0
    g3: LineSegment StartX=87.6 StartY=271.275 StartZ=0 EndX=87.6 EndY=258.5 EndZ=0
    g4: LineSegment StartX=12 StartY=258.5 StartZ=0 EndX=12 EndY=271.275 EndZ=0
    g5: LineSegment StartX=87.6 StartY=271.275 StartZ=0 EndX=87.1 EndY=271.775 EndZ=0
    g6: LineSegment StartX=12 StartY=271.275 StartZ=0 EndX=12.5 EndY=271.775 EndZ=0
    g7: LineSegment StartX=87.1 StartY=271.775 StartZ=0 EndX=85.0087 EndY=271.775 EndZ=0
    g8: LineSegment StartX=14.5913 StartY=271.775 StartZ=0 EndX=12.5 EndY=271.775 EndZ=0
    g9: ArcOfCircle CenterX=84.8352 CenterY=271.875 CenterZ=0 NormalX=0 NormalY=0 NormalZ=1 AngleXU=3.14159 Radius=0.200333 StartAngle=0 EndAngle=2.61799
    g10: ArcOfCircle CenterX=14.7648 CenterY=271.875 CenterZ=0 NormalX=0 NormalY=0 NormalZ=1 AngleXU=3.14159 Radius=0.200333 StartAngle=0.523599 EndAngle=4.18879
    g11: ArcOfCircle CenterX=84.8352 CenterY=271.875 CenterZ=0 NormalX=0 NormalY=0 NormalZ=1 AngleXU=3.14159 Radius=0.200333 StartAngle=5.23599 EndAngle=6.28319
    g12: LineSegment StartX=14.865 StartY=281.451 StartZ=0 EndX=14.865 EndY=272.049 EndZ=0
    g13: LineSegment StartX=84.735 StartY=281.451 StartZ=0 EndX=84.735 EndY=272.049 EndZ=0
    g14: ArcOfCircle CenterX=14.7648 CenterY=281.625 CenterZ=0 NormalX=0 NormalY=0 NormalZ=1 AngleXU=3.14159 Radius=0.200333 StartAngle=2.0944 EndAngle=5.75959
    g15: ArcOfCircle CenterX=84.8352 CenterY=281.625 CenterZ=0 NormalX=0 NormalY=0 NormalZ=1 AngleXU=3.14159 Radius=0.200333 StartAngle=0 EndAngle=1.0472
    g16: LineSegment StartX=14.5913 StartY=281.725 StartZ=0 EndX=12.5 EndY=281.725 EndZ=0
    g17: ArcOfCircle CenterX=84.8352 CenterY=281.625 CenterZ=0 NormalX=0 NormalY=0 NormalZ=1 AngleXU=3.14159 Radius=0.200333 StartAngle=3.66519 EndAngle=6.28319
    g18: LineSegment StartX=12.5 StartY=281.725 StartZ=0 EndX=12 EndY=282.225 EndZ=0
    g19: LineSegment StartX=87.1 StartY=281.725 StartZ=0 EndX=85.0087 EndY=281.725 EndZ=0
    g20: LineSegment StartX=87.6 StartY=282.225 StartZ=0 EndX=87.1 EndY=281.725 EndZ=0
    g21: LineSegment StartX=12 StartY=308.775 StartZ=0 EndX=12.5 EndY=309.275 EndZ=0
    g22: LineSegment StartX=87.6 StartY=308.775 StartZ=0 EndX=87.6 EndY=296.875 EndZ=0
    g23: LineSegment StartX=14.5913 StartY=309.275 StartZ=0 EndX=12.5 EndY=309.275 EndZ=0
    g24: LineSegment StartX=87.1 StartY=309.275 StartZ=0 EndX=87.6 EndY=308.775 EndZ=0
    g25: ArcOfCircle CenterX=14.7648 CenterY=309.375 CenterZ=0 NormalX=0 NormalY=0 NormalZ=1 AngleXU=3.14159 Radius=0.200333 StartAngle=0.523599 EndAngle=4.18879
    g26: LineSegment StartX=87.1 StartY=309.275 StartZ=0 EndX=85.0087 EndY=309.275 EndZ=0
    g27: LineSegment StartX=14.865 StartY=318.951 StartZ=0 EndX=14.865 EndY=309.549 EndZ=0
    g28: ArcOfCircle CenterX=84.8352 CenterY=309.375 CenterZ=0 NormalX=0 NormalY=0 NormalZ=1 AngleXU=3.14159 Radius=0.200333 StartAngle=0 EndAngle=2.61799
    g29: ArcOfCircle CenterX=14.7648 CenterY=319.125 CenterZ=0 NormalX=0 NormalY=0 NormalZ=1 AngleXU=3.14159 Radius=0.200333 StartAngle=2.0944 EndAngle=5.75959
    g30: ArcOfCircle CenterX=84.8352 CenterY=309.375 CenterZ=0 NormalX=0 NormalY=0 NormalZ=1 AngleXU=3.14159 Radius=0.200333 StartAngle=5.23599 EndAngle=6.28319
    g31: LineSegment StartX=14.5913 StartY=319.225 StartZ=0 EndX=12.5 EndY=319.225 EndZ=0
    g32: LineSegment StartX=84.735 StartY=318.951 StartZ=0 EndX=84.735 EndY=309.549 EndZ=0
    g33: LineSegment StartX=12.5 StartY=319.225 StartZ=0 EndX=12 EndY=319.725 EndZ=0
    g34: ArcOfCircle CenterX=84.8352 CenterY=319.125 CenterZ=0 NormalX=0 NormalY=0 NormalZ=1 AngleXU=3.14159 Radius=0.200333 StartAngle=0 EndAngle=1.0472
    g35: LineSegment StartX=12 StartY=319.725 StartZ=0 EndX=12 EndY=332.5 EndZ=0
    g36: ArcOfCircle CenterX=84.8352 CenterY=319.125 CenterZ=0 NormalX=0 NormalY=0 NormalZ=1 AngleXU=3.14159 Radius=0.200333 StartAngle=3.66519 EndAngle=6.28319
    g37: LineSegment StartX=12 StartY=332.5 StartZ=0 EndX=12.5 EndY=333 EndZ=0
    g38: LineSegment StartX=87.1 StartY=319.225 StartZ=0 EndX=85.0087 EndY=319.225 EndZ=0
    g39: LineSegment StartX=12.5 StartY=333 StartZ=0 EndX=33.1983 EndY=333 EndZ=0
    g40: LineSegment StartX=87.6 StartY=319.725 StartZ=0 EndX=87.1 EndY=319.225 EndZ=0
    g41: ArcOfCircle CenterX=33.385 CenterY=333 CenterZ=0 NormalX=0 NormalY=0 NormalZ=1 AngleXU=1.5708 Radius=0.186667 StartAngle=1.5708 EndAngle=4.71239
    g42: LineSegment StartX=87.6 StartY=332.5 StartZ=0 EndX=87.6 EndY=319.725 EndZ=0
    g43: ArcOfCircle CenterX=33.385 CenterY=333 CenterZ=0 NormalX=0 NormalY=0 NormalZ=1 AngleXU=1.5708 Radius=0.186667 StartAngle=4.71239 EndAngle=6.28319
    g44: LineSegment StartX=87.1 StartY=333 StartZ=0 EndX=87.6 EndY=332.5 EndZ=0
    g45: LineSegment StartX=33.385 StartY=333.187 StartZ=0 EndX=33.385 EndY=335.3 EndZ=0
    g46: LineSegment StartX=66.4017 StartY=333 StartZ=0 EndX=87.1 EndY=333 EndZ=0
    g47: LineSegment StartX=33.385 StartY=335.3 StartZ=0 EndX=33.885 EndY=335.8 EndZ=0
    g48: ArcOfCircle CenterX=66.215 CenterY=333 CenterZ=0 NormalX=0 NormalY=0 NormalZ=1 AngleXU=1.5708 Radius=0.186667 StartAngle=1.5708 EndAngle=4.71239
    g49: LineSegment StartX=43.035 StartY=335.8 StartZ=0 EndX=33.885 EndY=335.8 EndZ=0
    g50: ArcOfCircle CenterX=66.215 CenterY=333 CenterZ=0 NormalX=0 NormalY=0 NormalZ=1 AngleXU=1.5708 Radius=0.186667 StartAngle=0 EndAngle=1.5708
    g51: LineSegment StartX=43.035 StartY=335.8 StartZ=0 EndX=43.535 EndY=335.3 EndZ=0
    g52: LineSegment StartX=66.215 StartY=333.187 StartZ=0 EndX=66.215 EndY=335.3 EndZ=0
    g53: LineSegment StartX=43.535 StartY=333.187 StartZ=0 EndX=43.535 EndY=335.3 EndZ=0
    g54: LineSegment StartX=65.715 StartY=335.8 StartZ=0 EndX=66.215 EndY=335.3 EndZ=0
    g55: ArcOfCircle CenterX=43.535 CenterY=333 CenterZ=0 NormalX=0 NormalY=0 NormalZ=1 AngleXU=1.5708 Radius=0.186667 StartAngle=0 EndAngle=1.5708
    g56: LineSegment StartX=65.715 StartY=335.8 StartZ=0 EndX=56.565 EndY=335.8 EndZ=0
    g57: ArcOfCircle CenterX=43.535 CenterY=333 CenterZ=0 NormalX=0 NormalY=0 NormalZ=1 AngleXU=1.5708 Radius=0.186667 StartAngle=1.5708 EndAngle=4.71239
    g58: LineSegment StartX=56.065 StartY=335.3 StartZ=0 EndX=56.565 EndY=335.8 EndZ=0
    g59: LineSegment StartX=43.7217 StartY=333 StartZ=0 EndX=55.8783 EndY=333 EndZ=0
    g60: LineSegment StartX=56.065 StartY=333.187 StartZ=0 EndX=56.065 EndY=335.3 EndZ=0
    g61: ArcOfCircle CenterX=56.065 CenterY=333 CenterZ=0 NormalX=0 NormalY=0 NormalZ=1 AngleXU=1.5708 Radius=0.186667 StartAngle=1.5708 EndAngle=4.71239
    g62: ArcOfCircle CenterX=56.065 CenterY=333 CenterZ=0 NormalX=0 NormalY=0 NormalZ=1 AngleXU=1.5708 Radius=0.186667 StartAngle=4.71239 EndAngle=6.28319
    g63: LineSegment StartX=12 StartY=282.225 StartZ=0 EndX=12 EndY=295.875 EndZ=0
    g64: LineSegment StartX=12 StartY=296.875 StartZ=0 EndX=12 EndY=308.775 EndZ=0
    g65: LineSegment StartX=87.6 StartY=295.875 StartZ=0 EndX=87.6 EndY=282.225 EndZ=0
    g66: LineSegment StartX=48.4 StartY=306 StartZ=0 EndX=48.4 EndY=296 EndZ=0
    g67: LineSegment StartX=48.4 StartY=296 StartZ=0 EndX=51.2 EndY=296 EndZ=0
    g68: LineSegment StartX=51.2 StartY=296 StartZ=0 EndX=51.2 EndY=306 EndZ=0
    g69: LineSegment StartX=51.2 StartY=306 StartZ=0 EndX=48.4 EndY=306 EndZ=0
    g70: GeomPoint [constr] X=49.8 Y=301 Z=0
    g71: LineSegment [constr] StartX=49.8 StartY=306 StartZ=0 EndX=49.8 EndY=333 EndZ=0
  constraints (25):
    c: Coincident(g63,g18)
    c: Vertical(g63)
    c: Coincident(g65,g20)
    c: Vertical(g65)
    c: Coincident(g66,g67)
    c: Coincident(g67,g68)
    c: Coincident(g68,g69)
    c: Coincident(g69,g66)
    c: Vertical(g66)
    c: Vertical(g68)
    c: Horizontal(g67)
    c: Horizontal(g69)
    c: Symmetric(g68,g66,g70)
    c: Distance(g67,g67) = 2.8
    c: DistanceY(g66,g66) = 10
    c: DistanceX(g59) = 43.7217
    c: DistanceY(g59) = 333
    c: DistanceX(g59) = 55.8783
    c: DistanceY(g59) = 333
    c: Symmetric(g69,g69,g71)
    c: Symmetric(g59,g59,g71)
    c: Vertical(g71)
    c: DistanceX(g0) = 87.1
    c: DistanceY(g0) = 258
    c: DistanceY(g0,g67) = 38
FEATURE [Sketcher::SketchObject] Sketch006
  ArcFitTolerance = 1e-06
  FullyConstrained = false
  MakeInternals = false
  sketch-geometry (84):
    g0: LineSegment StartX=113.5 StartY=305.965 StartZ=0 EndX=115.591 EndY=305.965 EndZ=0
    g1: LineSegment StartX=113.5 StartY=305.965 StartZ=0 EndX=113 EndY=305.465 EndZ=0
    g2: ArcOfCircle CenterX=115.765 CenterY=306.065 CenterZ=0 NormalX=0 NormalY=0 NormalZ=1 AngleXU=-1e-16 Radius=0.200333 StartAngle=0 EndAngle=1.0472
    g3: ArcOfCircle CenterX=115.765 CenterY=306.065 CenterZ=0 NormalX=0 NormalY=0 NormalZ=1 AngleXU=-1e-16 Radius=0.200333 StartAngle=3.66519 EndAngle=6.28319
    g4: LineSegment StartX=113 StartY=316.415 StartZ=0 EndX=113.5 EndY=315.915 EndZ=0
    g5: LineSegment StartX=113.5 StartY=326.2 StartZ=0 EndX=113 EndY=325.7 EndZ=0
    g6: LineSegment StartX=113.5 StartY=315.915 StartZ=0 EndX=115.591 EndY=315.915 EndZ=0
    g7: LineSegment StartX=113.5 StartY=326.2 StartZ=0 EndX=134.198 EndY=326.2 EndZ=0
    g8: ArcOfCircle CenterX=115.765 CenterY=315.815 CenterZ=0 NormalX=0 NormalY=0 NormalZ=1 AngleXU=-1e-16 Radius=0.200333 StartAngle=0 EndAngle=2.61799
    g9: ArcOfCircle CenterX=134.385 CenterY=326.2 CenterZ=0 NormalX=0 NormalY=0 NormalZ=1 AngleXU=1.5708 Radius=0.186667 StartAngle=1.5708 EndAngle=4.71239
    g10: ArcOfCircle CenterX=115.765 CenterY=315.815 CenterZ=0 NormalX=0 NormalY=0 NormalZ=1 AngleXU=-1e-16 Radius=0.200333 StartAngle=5.23599 EndAngle=6.28319
    g11: ArcOfCircle CenterX=134.385 CenterY=326.2 CenterZ=0 NormalX=0 NormalY=0 NormalZ=1 AngleXU=1.5708 Radius=0.186667 StartAngle=4.71239 EndAngle=6.28319
    g12: LineSegment StartX=115.865 StartY=306.239 StartZ=0 EndX=115.865 EndY=311.228 EndZ=0
    g13: LineSegment StartX=134.385 StartY=326.387 StartZ=0 EndX=134.385 EndY=328.5 EndZ=0
    g14: LineSegment StartX=134.885 StartY=329 StartZ=0 EndX=134.385 EndY=328.5 EndZ=0
    g15: LineSegment StartX=144.035 StartY=329 StartZ=0 EndX=134.885 EndY=329 EndZ=0
    g16: LineSegment StartX=144.535 StartY=328.5 StartZ=0 EndX=144.035 EndY=329 EndZ=0
    g17: LineSegment StartX=144.535 StartY=326.387 StartZ=0 EndX=144.535 EndY=328.5 EndZ=0
    g18: LineSegment StartX=113 StartY=299.16 StartZ=0 EndX=113 EndY=305.465 EndZ=0
    g19: ArcOfCircle CenterX=144.535 CenterY=326.2 CenterZ=0 NormalX=0 NormalY=0 NormalZ=1 AngleXU=1.5708 Radius=0.186667 StartAngle=0 EndAngle=1.5708
    g20: LineSegment StartX=113 StartY=299.16 StartZ=0 EndX=113.5 EndY=298.66 EndZ=0
    g21: ArcOfCircle CenterX=144.535 CenterY=326.2 CenterZ=0 NormalX=0 NormalY=0 NormalZ=1 AngleXU=1.5708 Radius=0.186667 StartAngle=1.5708 EndAngle=4.71239
    g22: LineSegment StartX=126.638 StartY=298.66 StartZ=0 EndX=113.5 EndY=298.66 EndZ=0
    g23: LineSegment StartX=144.722 StartY=326.2 StartZ=0 EndX=156.878 EndY=326.2 EndZ=0
    g24: ArcOfCircle CenterX=126.825 CenterY=298.66 CenterZ=0 NormalX=0 NormalY=0 NormalZ=1 AngleXU=-1.5708 Radius=0.186667 StartAngle=1.5708 EndAngle=4.71239
    g25: ArcOfCircle CenterX=157.065 CenterY=326.2 CenterZ=0 NormalX=0 NormalY=0 NormalZ=1 AngleXU=1.5708 Radius=0.186667 StartAngle=1.5708 EndAngle=4.71239
    g26: ArcOfCircle CenterX=126.825 CenterY=298.66 CenterZ=0 NormalX=0 NormalY=0 NormalZ=1 AngleXU=-1.5708 Radius=0.186667 StartAngle=0 EndAngle=1.5708
    g27: ArcOfCircle CenterX=157.065 CenterY=326.2 CenterZ=0 NormalX=0 NormalY=0 NormalZ=1 AngleXU=1.5708 Radius=0.186667 StartAngle=4.71239 EndAngle=6.28319
    g28: LineSegment StartX=126.825 StartY=298.473 StartZ=0 EndX=126.825 EndY=296.36 EndZ=0
    g29: LineSegment StartX=157.065 StartY=326.387 StartZ=0 EndX=157.065 EndY=328.5 EndZ=0
    g30: LineSegment StartX=126.825 StartY=296.36 StartZ=0 EndX=127.325 EndY=295.86 EndZ=0
    g31: LineSegment StartX=157.565 StartY=329 StartZ=0 EndX=157.065 EndY=328.5 EndZ=0
    g32: LineSegment StartX=127.325 StartY=295.86 StartZ=0 EndX=136.475 EndY=295.86 EndZ=0
    g33: LineSegment StartX=166.715 StartY=329 StartZ=0 EndX=157.565 EndY=329 EndZ=0
    g34: LineSegment StartX=136.475 StartY=295.86 StartZ=0 EndX=136.975 EndY=296.36 EndZ=0
    g35: LineSegment StartX=167.215 StartY=328.5 StartZ=0 EndX=166.715 EndY=329 EndZ=0
    g36: LineSegment StartX=136.975 StartY=298.473 StartZ=0 EndX=136.975 EndY=296.36 EndZ=0
    g37: LineSegment StartX=167.215 StartY=326.387 StartZ=0 EndX=167.215 EndY=328.5 EndZ=0
    g38: ArcOfCircle CenterX=136.975 CenterY=298.66 CenterZ=0 NormalX=0 NormalY=0 NormalZ=1 AngleXU=-1.5708 Radius=0.186667 StartAngle=4.71239 EndAngle=6.28319
    g39: ArcOfCircle CenterX=167.215 CenterY=326.2 CenterZ=0 NormalX=0 NormalY=0 NormalZ=1 AngleXU=1.5708 Radius=0.186667 StartAngle=0 EndAngle=1.5708
    g40: ArcOfCircle CenterX=136.975 CenterY=298.66 CenterZ=0 NormalX=0 NormalY=0 NormalZ=1 AngleXU=-1.5708 Radius=0.186667 StartAngle=1.5708 EndAngle=4.71239
    g41: ArcOfCircle CenterX=167.215 CenterY=326.2 CenterZ=0 NormalX=0 NormalY=0 NormalZ=1 AngleXU=1.5708 Radius=0.186667 StartAngle=1.5708 EndAngle=4.71239
    g42: LineSegment StartX=164.438 StartY=298.66 StartZ=0 EndX=137.162 EndY=298.66 EndZ=0
    g43: LineSegment StartX=167.402 StartY=326.2 StartZ=0 EndX=188.1 EndY=326.2 EndZ=0
    g44: ArcOfCircle CenterX=164.625 CenterY=298.66 CenterZ=0 NormalX=0 NormalY=0 NormalZ=1 AngleXU=-1.5708 Radius=0.186667 StartAngle=1.5708 EndAngle=4.71239
    g45: LineSegment StartX=188.6 StartY=325.7 StartZ=0 EndX=188.1 EndY=326.2 EndZ=0
    g46: ArcOfCircle CenterX=164.625 CenterY=298.66 CenterZ=0 NormalX=0 NormalY=0 NormalZ=1 AngleXU=-1.5708 Radius=0.186667 StartAngle=0 EndAngle=1.5708
    g47: LineSegment StartX=164.625 StartY=298.473 StartZ=0 EndX=164.625 EndY=296.36 EndZ=0
    g48: LineSegment StartX=188.1 StartY=315.915 StartZ=0 EndX=188.6 EndY=316.415 EndZ=0
    g49: LineSegment StartX=164.625 StartY=296.36 StartZ=0 EndX=165.125 EndY=295.86 EndZ=0
    g50: LineSegment StartX=186.009 StartY=315.915 StartZ=0 EndX=188.1 EndY=315.915 EndZ=0
    g51: LineSegment StartX=165.125 StartY=295.86 StartZ=0 EndX=174.275 EndY=295.86 EndZ=0
    g52: ArcOfCircle CenterX=185.835 CenterY=315.815 CenterZ=0 NormalX=0 NormalY=0 NormalZ=1 AngleXU=-1e-16 Radius=0.200333 StartAngle=0.523599 EndAngle=4.18879
    g53: LineSegment StartX=174.275 StartY=295.86 StartZ=0 EndX=174.775 EndY=296.36 EndZ=0
    g54: LineSegment StartX=185.735 StartY=306.239 StartZ=0 EndX=185.735 EndY=311.228 EndZ=0
    g55: LineSegment StartX=174.775 StartY=298.473 StartZ=0 EndX=174.775 EndY=296.36 EndZ=0
    g56: ArcOfCircle CenterX=185.835 CenterY=306.065 CenterZ=0 NormalX=0 NormalY=0 NormalZ=1 AngleXU=-1e-16 Radius=0.200333 StartAngle=2.0944 EndAngle=5.75959
    g57: ArcOfCircle CenterX=174.775 CenterY=298.66 CenterZ=0 NormalX=0 NormalY=0 NormalZ=1 AngleXU=-1.5708 Radius=0.186667 StartAngle=4.71239 EndAngle=6.28319
    g58: LineSegment StartX=186.009 StartY=305.965 StartZ=0 EndX=188.1 EndY=305.965 EndZ=0
    g59: ArcOfCircle CenterX=174.775 CenterY=298.66 CenterZ=0 NormalX=0 NormalY=0 NormalZ=1 AngleXU=-1.5708 Radius=0.186667 StartAngle=1.5708 EndAngle=4.71239
    g60: LineSegment StartX=188.6 StartY=305.465 StartZ=0 EndX=188.1 EndY=305.965 EndZ=0
    g61: LineSegment StartX=188.1 StartY=298.66 StartZ=0 EndX=174.962 EndY=298.66 EndZ=0
    g62: LineSegment StartX=188.6 StartY=305.465 StartZ=0 EndX=188.6 EndY=299.16 EndZ=0
    g63: LineSegment StartX=188.1 StartY=298.66 StartZ=0 EndX=188.6 EndY=299.16 EndZ=0
    g64: Circle CenterX=150.785 CenterY=309.466 CenterZ=0 NormalX=0 NormalY=0 NormalZ=-1 AngleXU=1e-16 Radius=7.5
    g65: LineSegment StartX=170.365 StartY=316.49 StartZ=0 EndX=168.008 EndY=310.49 EndZ=0
    g66: ArcOfCircle CenterX=164.75 CenterY=311.77 CenterZ=0 NormalX=0 NormalY=0 NormalZ=1 AngleXU=3.14159 Radius=3.5 StartAngle=0.365625 EndAngle=2.76729
    g67: LineSegment StartX=161.481 StartY=310.519 StartZ=0 EndX=159.177 EndY=316.539 EndZ=0
    g68: ArcOfCircle CenterX=164.78 CenterY=318.684 CenterZ=0 NormalX=0 NormalY=0 NormalZ=1 AngleXU=3.14159 Radius=6 StartAngle=2.76729 EndAngle=6.64881
    g69: Circle CenterX=123.76 CenterY=316.05 CenterZ=0 NormalX=0 NormalY=0 NormalZ=-1 AngleXU=1e-16 Radius=5
    g70: Circle CenterX=177.84 CenterY=315.95 CenterZ=0 NormalX=0 NormalY=0 NormalZ=-1 AngleXU=1e-16 Radius=5
    g71: Circle CenterX=133.782 CenterY=314.038 CenterZ=0 NormalX=0 NormalY=0 NormalZ=-1 AngleXU=1e-16 Radius=3
    g72: ArcOfCircle CenterX=139.37 CenterY=316.05 CenterZ=0 NormalX=0 NormalY=0 NormalZ=1 AngleXU=3.14159 Radius=1.5 StartAngle=3.14159 EndAngle=6.28319
    g73: LineSegment StartX=140.87 StartY=316.05 StartZ=0 EndX=140.87 EndY=313.55 EndZ=0
    g74: ArcOfCircle CenterX=139.37 CenterY=313.55 CenterZ=0 NormalX=0 NormalY=0 NormalZ=1 AngleXU=3.14159 Radius=1.5 StartAngle=9e-16 EndAngle=3.14159
    g75: LineSegment StartX=137.87 StartY=316.05 StartZ=0 EndX=137.87 EndY=313.55 EndZ=0
    g76: LineSegment StartX=115.865 StartY=312.228 StartZ=0 EndX=115.865 EndY=315.641 EndZ=0
    g77: LineSegment StartX=185.735 StartY=312.228 StartZ=0 EndX=185.735 EndY=315.641 EndZ=0
    g78: LineSegment StartX=115.865 StartY=311.228 StartZ=0 EndX=115.865 EndY=312.228 EndZ=0
    g79: LineSegment StartX=185.735 StartY=311.228 StartZ=0 EndX=185.735 EndY=312.228 EndZ=0
    g80: LineSegment StartX=113 StartY=325.7 StartZ=0 EndX=113 EndY=317.702 EndZ=0
    g81: LineSegment StartX=113 StartY=316.705 StartZ=0 EndX=113 EndY=316.415 EndZ=0
    g82: LineSegment StartX=188.6 StartY=325.7 StartZ=0 EndX=188.6 EndY=317.699 EndZ=0
    g83: LineSegment StartX=188.6 StartY=316.701 StartZ=0 EndX=188.6 EndY=316.415 EndZ=0
  constraints (14):
    c: Coincident(g78,g12)
    c: Coincident(g78,g76)
    c: Vertical(g78)
    c: Coincident(g79,g54)
    c: Coincident(g79,g77)
    c: Vertical(g79)
    c: Coincident(g80,g5)
    c: Vertical(g80)
    c: Coincident(g81,g4)
    c: Vertical(g81)
    c: Coincident(g82,g45)
    c: Vertical(g82)
    c: Coincident(g83,g48)
    c: Vertical(g83)
FEATURE [Sketcher::SketchObject] Sketch007
  ArcFitTolerance = 1e-06
  FullyConstrained = false
  MakeInternals = false
  sketch-geometry (30):
    g0: LineSegment StartX=87.1 StartY=177.077 StartZ=0 EndX=12.5 EndY=177.077 EndZ=0
    g1: LineSegment StartX=87.6 StartY=191.7 StartZ=0 EndX=87.6 EndY=185.413 EndZ=0
    g2: LineSegment StartX=87.6 StartY=191.7 StartZ=0 EndX=87.1 EndY=192.2 EndZ=0
    g3: LineSegment StartX=87.1 StartY=177.077 StartZ=0 EndX=87.6 EndY=177.577 EndZ=0
    g4: LineSegment StartX=73.9617 StartY=192.2 StartZ=0 EndX=87.1 EndY=192.2 EndZ=0
    g5: ArcOfCircle CenterX=73.775 CenterY=192.2 CenterZ=0 NormalX=0 NormalY=0 NormalZ=1 AngleXU=1.5708 Radius=0.186667 StartAngle=1.5708 EndAngle=4.71239
    g6: LineSegment StartX=12.5 StartY=177.077 StartZ=0 EndX=12 EndY=177.577 EndZ=0
    g7: ArcOfCircle CenterX=73.775 CenterY=192.2 CenterZ=0 NormalX=0 NormalY=0 NormalZ=1 AngleXU=1.5708 Radius=0.186667 StartAngle=0 EndAngle=1.5708
    g8: LineSegment StartX=12 StartY=177.577 StartZ=0 EndX=12 EndY=184.413 EndZ=0
    g9: LineSegment StartX=73.775 StartY=192.387 StartZ=0 EndX=73.775 EndY=194.5 EndZ=0
    g10: LineSegment StartX=12 StartY=191.7 StartZ=0 EndX=12.5 EndY=192.2 EndZ=0
    g11: LineSegment StartX=73.775 StartY=194.5 StartZ=0 EndX=73.275 EndY=195 EndZ=0
    g12: LineSegment StartX=12.5 StartY=192.2 StartZ=0 EndX=25.6383 EndY=192.2 EndZ=0
    g13: LineSegment StartX=73.275 StartY=195 StartZ=0 EndX=64.125 EndY=195 EndZ=0
    g14: ArcOfCircle CenterX=25.825 CenterY=192.2 CenterZ=0 NormalX=0 NormalY=0 NormalZ=1 AngleXU=1.5708 Radius=0.186667 StartAngle=1.5708 EndAngle=4.71239
    g15: LineSegment StartX=64.125 StartY=195 StartZ=0 EndX=63.625 EndY=194.5 EndZ=0
    g16: ArcOfCircle CenterX=25.825 CenterY=192.2 CenterZ=0 NormalX=0 NormalY=0 NormalZ=1 AngleXU=1.5708 Radius=0.186667 StartAngle=4.71239 EndAngle=6.28319
    g17: LineSegment StartX=63.625 StartY=192.387 StartZ=0 EndX=63.625 EndY=194.5 EndZ=0
    g18: LineSegment StartX=25.825 StartY=192.387 StartZ=0 EndX=25.825 EndY=194.5 EndZ=0
    g19: ArcOfCircle CenterX=63.625 CenterY=192.2 CenterZ=0 NormalX=0 NormalY=0 NormalZ=1 AngleXU=1.5708 Radius=0.186667 StartAngle=4.71239 EndAngle=6.28319
    g20: LineSegment StartX=25.825 StartY=194.5 StartZ=0 EndX=26.325 EndY=195 EndZ=0
    g21: ArcOfCircle CenterX=63.625 CenterY=192.2 CenterZ=0 NormalX=0 NormalY=0 NormalZ=1 AngleXU=1.5708 Radius=0.186667 StartAngle=1.5708 EndAngle=4.71239
    g22: LineSegment StartX=35.475 StartY=195 StartZ=0 EndX=26.325 EndY=195 EndZ=0
    g23: LineSegment StartX=36.1617 StartY=192.2 StartZ=0 EndX=63.4383 EndY=192.2 EndZ=0
    g24: LineSegment StartX=35.975 StartY=194.5 StartZ=0 EndX=35.475 EndY=195 EndZ=0
    g25: ArcOfCircle CenterX=35.975 CenterY=192.2 CenterZ=0 NormalX=0 NormalY=0 NormalZ=1 AngleXU=1.5708 Radius=0.186667 StartAngle=1.5708 EndAngle=4.71239
    g26: LineSegment StartX=35.975 StartY=192.387 StartZ=0 EndX=35.975 EndY=194.5 EndZ=0
    g27: ArcOfCircle CenterX=35.975 CenterY=192.2 CenterZ=0 NormalX=0 NormalY=0 NormalZ=1 AngleXU=1.5708 Radius=0.186667 StartAngle=0 EndAngle=1.5708
    g28: LineSegment StartX=12 StartY=185.413 StartZ=0 EndX=12 EndY=191.7 EndZ=0
    g29: LineSegment StartX=87.6 StartY=184.413 StartZ=0 EndX=87.6 EndY=177.577 EndZ=0
FEATURE [Sketcher::SketchObject] Sketch008
  ArcFitTolerance = 1e-06
  FullyConstrained = false
  MakeInternals = false
  sketch-geometry (125):
    g0: LineSegment StartX=188.6 StartY=285.6 StartZ=0 EndX=188.6 EndY=268.525 EndZ=0
    g1: LineSegment StartX=188.6 StartY=268.525 StartZ=0 EndX=188.1 EndY=268.025 EndZ=0
    g2: ArcOfCircle CenterX=188.2 CenterY=285.6 CenterZ=0 NormalX=0 NormalY=0 NormalZ=1 AngleXU=-1e-16 Radius=0.4 StartAngle=0 EndAngle=1.5708
    g3: LineSegment StartX=188.1 StartY=268.025 StartZ=0 EndX=186.009 EndY=268.025 EndZ=0
    g4: LineSegment StartX=174.6 StartY=286 StartZ=0 EndX=188.2 EndY=286 EndZ=0
    g5: ArcOfCircle CenterX=185.835 CenterY=267.925 CenterZ=0 NormalX=0 NormalY=0 NormalZ=1 AngleXU=3.14159 Radius=0.200333 StartAngle=3.66519 EndAngle=6.28319
    g6: ArcOfCircle CenterX=174.6 CenterY=286.4 CenterZ=0 NormalX=0 NormalY=0 NormalZ=1 AngleXU=-1e-16 Radius=0.4 StartAngle=1.5708 EndAngle=4.71239
    g7: ArcOfCircle CenterX=185.835 CenterY=267.925 CenterZ=0 NormalX=0 NormalY=0 NormalZ=1 AngleXU=3.14159 Radius=0.200333 StartAngle=0 EndAngle=1.0472
    g8: LineSegment StartX=188.2 StartY=286.8 StartZ=0 EndX=174.6 EndY=286.8 EndZ=0
    g9: LineSegment StartX=185.735 StartY=258.349 StartZ=0 EndX=185.735 EndY=267.751 EndZ=0
    g10: ArcOfCircle CenterX=188.2 CenterY=287.2 CenterZ=0 NormalX=0 NormalY=0 NormalZ=1 AngleXU=-1e-16 Radius=0.4 StartAngle=4.71239 EndAngle=6.28319
    g11: ArcOfCircle CenterX=185.835 CenterY=258.175 CenterZ=0 NormalX=0 NormalY=0 NormalZ=1 AngleXU=3.14159 Radius=0.200333 StartAngle=5.23599 EndAngle=6.28319
    g12: LineSegment StartX=188.6 StartY=289.353 StartZ=0 EndX=188.6 EndY=287.2 EndZ=0
    g13: ArcOfCircle CenterX=185.835 CenterY=258.175 CenterZ=0 NormalX=0 NormalY=0 NormalZ=1 AngleXU=3.14159 Radius=0.200333 StartAngle=0 EndAngle=2.61799
    g14: ArcOfCircle CenterX=188.2 CenterY=289.353 CenterZ=0 NormalX=0 NormalY=0 NormalZ=1 AngleXU=-1e-16 Radius=0.4 StartAngle=0 EndAngle=1.10715
    g15: LineSegment StartX=188.1 StartY=258.075 StartZ=0 EndX=186.009 EndY=258.075 EndZ=0
    g16: LineSegment StartX=188.379 StartY=289.711 StartZ=0 EndX=186.6 EndY=290.6 EndZ=0
    g17: LineSegment StartX=188.1 StartY=258.075 StartZ=0 EndX=188.6 EndY=257.575 EndZ=0
    g18: LineSegment StartX=186.6 StartY=290.6 StartZ=0 EndX=186.6 EndY=289.6 EndZ=0
    g19: LineSegment StartX=188.6 StartY=257.575 StartZ=0 EndX=188.6 EndY=240.322 EndZ=0
    g20: LineSegment StartX=186.6 StartY=289.6 StartZ=0 EndX=183.8 EndY=289.6 EndZ=0
    g21: LineSegment StartX=188.6 StartY=221.025 StartZ=0 EndX=188.1 EndY=220.525 EndZ=0
    g22: LineSegment StartX=183.8 StartY=289.6 StartZ=0 EndX=183.8 EndY=291.6 EndZ=0
    g23: LineSegment StartX=188.1 StartY=220.525 StartZ=0 EndX=186.009 EndY=220.525 EndZ=0
    g24: LineSegment StartX=183.8 StartY=291.6 StartZ=0 EndX=176.387 EndY=289.614 EndZ=0
    g25: ArcOfCircle CenterX=185.835 CenterY=220.425 CenterZ=0 NormalX=0 NormalY=0 NormalZ=1 AngleXU=3.14159 Radius=0.200333 StartAngle=3.66519 EndAngle=6.28319
    g26: ArcOfCircle CenterX=176.283 CenterY=290 CenterZ=0 NormalX=0 NormalY=0 NormalZ=1 AngleXU=-1e-16 Radius=0.4 StartAngle=4.71239 EndAngle=4.97419
    g27: ArcOfCircle CenterX=185.835 CenterY=220.425 CenterZ=0 NormalX=0 NormalY=0 NormalZ=1 AngleXU=3.14159 Radius=0.200333 StartAngle=0 EndAngle=1.0472
    g28: LineSegment StartX=176.283 StartY=289.6 StartZ=0 EndX=156.275 EndY=289.6 EndZ=0
    g29: LineSegment StartX=185.735 StartY=210.849 StartZ=0 EndX=185.735 EndY=220.251 EndZ=0
    g30: LineSegment StartX=155.775 StartY=289.1 StartZ=0 EndX=156.275 EndY=289.6 EndZ=0
    g31: ArcOfCircle CenterX=185.835 CenterY=210.675 CenterZ=0 NormalX=0 NormalY=0 NormalZ=1 AngleXU=3.14159 Radius=0.200333 StartAngle=5.23599 EndAngle=6.28319
    g32: LineSegment StartX=155.775 StartY=289.1 StartZ=0 EndX=155.775 EndY=287.009 EndZ=0
    g33: ArcOfCircle CenterX=185.835 CenterY=210.675 CenterZ=0 NormalX=0 NormalY=0 NormalZ=1 AngleXU=3.14159 Radius=0.200333 StartAngle=0 EndAngle=2.61799
    g34: ArcOfCircle CenterX=155.675 CenterY=286.835 CenterZ=0 NormalX=0 NormalY=0 NormalZ=1 AngleXU=-1.5708 Radius=0.200333 StartAngle=0 EndAngle=2.61799
    g35: LineSegment StartX=188.1 StartY=210.575 StartZ=0 EndX=186.009 EndY=210.575 EndZ=0
    g36: ArcOfCircle CenterX=155.675 CenterY=286.835 CenterZ=0 NormalX=0 NormalY=0 NormalZ=1 AngleXU=-1.5708 Radius=0.200333 StartAngle=5.23599 EndAngle=6.28319
    g37: LineSegment StartX=188.1 StartY=210.575 StartZ=0 EndX=188.6 EndY=210.075 EndZ=0
    g38: LineSegment StartX=155.501 StartY=286.735 StartZ=0 EndX=146.099 EndY=286.735 EndZ=0
    g39: LineSegment StartX=188.6 StartY=210.075 StartZ=0 EndX=188.6 EndY=193 EndZ=0
    g40: ArcOfCircle CenterX=145.925 CenterY=286.835 CenterZ=0 NormalX=0 NormalY=0 NormalZ=1 AngleXU=-1.5708 Radius=0.200333 StartAngle=0 EndAngle=1.0472
    g41: ArcOfCircle CenterX=188.2 CenterY=193 CenterZ=0 NormalX=0 NormalY=0 NormalZ=1 AngleXU=-1e-16 Radius=0.4 StartAngle=4.71239 EndAngle=6.28319
    g42: ArcOfCircle CenterX=145.925 CenterY=286.835 CenterZ=0 NormalX=0 NormalY=0 NormalZ=1 AngleXU=-1.5708 Radius=0.200333 StartAngle=3.66519 EndAngle=6.28319
    g43: LineSegment StartX=188.2 StartY=192.6 StartZ=0 EndX=174.6 EndY=192.6 EndZ=0
    g44: LineSegment StartX=145.825 StartY=289.1 StartZ=0 EndX=145.825 EndY=287.009 EndZ=0
    g45: ArcOfCircle CenterX=174.6 CenterY=192.2 CenterZ=0 NormalX=0 NormalY=0 NormalZ=1 AngleXU=-1e-16 Radius=0.4 StartAngle=1.5708 EndAngle=4.71239
    g46: LineSegment StartX=145.325 StartY=289.6 StartZ=0 EndX=145.825 EndY=289.1 EndZ=0
    g47: LineSegment StartX=174.6 StartY=191.8 StartZ=0 EndX=188.2 EndY=191.8 EndZ=0
    g48: LineSegment StartX=145.325 StartY=289.6 StartZ=0 EndX=125.317 EndY=289.6 EndZ=0
    g49: ArcOfCircle CenterX=188.2 CenterY=191.4 CenterZ=0 NormalX=0 NormalY=0 NormalZ=1 AngleXU=-1e-16 Radius=0.4 StartAngle=0 EndAngle=1.5708
    g50: ArcOfCircle CenterX=125.317 CenterY=290 CenterZ=0 NormalX=0 NormalY=0 NormalZ=1 AngleXU=-1e-16 Radius=0.4 StartAngle=4.45059 EndAngle=4.71239
    g51: LineSegment StartX=188.6 StartY=191.4 StartZ=0 EndX=188.6 EndY=189.247 EndZ=0
    g52: LineSegment StartX=125.213 StartY=289.614 StartZ=0 EndX=117.8 EndY=291.6 EndZ=0
    g53: ArcOfCircle CenterX=188.2 CenterY=189.247 CenterZ=0 NormalX=0 NormalY=0 NormalZ=1 AngleXU=-1e-16 Radius=0.4 StartAngle=5.17604 EndAngle=6.28319
    g54: LineSegment StartX=117.8 StartY=291.6 StartZ=0 EndX=117.8 EndY=289.6 EndZ=0
    g55: LineSegment StartX=188.379 StartY=188.889 StartZ=0 EndX=186.6 EndY=188 EndZ=0
    g56: LineSegment StartX=115 StartY=289.6 StartZ=0 EndX=117.8 EndY=289.6 EndZ=0
    g57: LineSegment StartX=186.6 StartY=188 StartZ=0 EndX=186.6 EndY=189 EndZ=0
    g58: LineSegment StartX=115 StartY=290.6 StartZ=0 EndX=115 EndY=289.6 EndZ=0
    g59: LineSegment StartX=186.6 StartY=189 StartZ=0 EndX=183.8 EndY=189 EndZ=0
    g60: LineSegment StartX=113.221 StartY=289.711 StartZ=0 EndX=115 EndY=290.6 EndZ=0
    g61: LineSegment StartX=183.8 StartY=187 StartZ=0 EndX=183.8 EndY=189 EndZ=0
    g62: ArcOfCircle CenterX=113.4 CenterY=289.353 CenterZ=0 NormalX=0 NormalY=0 NormalZ=1 AngleXU=-1e-16 Radius=0.4 StartAngle=2.03444 EndAngle=3.14159
    g63: LineSegment StartX=176.387 StartY=188.986 StartZ=0 EndX=183.8 EndY=187 EndZ=0
    g64: LineSegment StartX=113 StartY=287.2 StartZ=0 EndX=113 EndY=289.353 EndZ=0
    g65: ArcOfCircle CenterX=176.283 CenterY=188.6 CenterZ=0 NormalX=0 NormalY=0 NormalZ=1 AngleXU=-1e-16 Radius=0.4 StartAngle=1.309 EndAngle=1.5708
    g66: ArcOfCircle CenterX=113.4 CenterY=287.2 CenterZ=0 NormalX=0 NormalY=0 NormalZ=1 AngleXU=-1e-16 Radius=0.4 StartAngle=3.14159 EndAngle=4.71239
    g67: LineSegment StartX=125.317 StartY=189 StartZ=0 EndX=176.283 EndY=189 EndZ=0
    g68: LineSegment StartX=113.4 StartY=286.8 StartZ=0 EndX=127 EndY=286.8 EndZ=0
    g69: ArcOfCircle CenterX=125.317 CenterY=188.6 CenterZ=0 NormalX=0 NormalY=0 NormalZ=1 AngleXU=-1e-16 Radius=0.4 StartAngle=1.5708 EndAngle=1.8326
    g70: ArcOfCircle CenterX=127 CenterY=286.4 CenterZ=0 NormalX=0 NormalY=0 NormalZ=1 AngleXU=-1e-16 Radius=0.4 StartAngle=4.71239 EndAngle=7.85398
    g71: LineSegment StartX=117.8 StartY=187 StartZ=0 EndX=125.213 EndY=188.986 EndZ=0
    g72: LineSegment StartX=127 StartY=286 StartZ=0 EndX=113.4 EndY=286 EndZ=0
    g73: LineSegment StartX=117.8 StartY=189 StartZ=0 EndX=117.8 EndY=187 EndZ=0
    g74: ArcOfCircle CenterX=113.4 CenterY=285.6 CenterZ=0 NormalX=0 NormalY=0 NormalZ=1 AngleXU=-1e-16 Radius=0.4 StartAngle=1.5708 EndAngle=3.14159
    g75: LineSegment StartX=115 StartY=189 StartZ=0 EndX=117.8 EndY=189 EndZ=0
    g76: LineSegment StartX=113 StartY=268.525 StartZ=0 EndX=113 EndY=285.6 EndZ=0
    g77: LineSegment StartX=115 StartY=188 StartZ=0 EndX=115 EndY=189 EndZ=0
    g78: LineSegment StartX=113.5 StartY=268.025 StartZ=0 EndX=113 EndY=268.525 EndZ=0
    g79: LineSegment StartX=113.221 StartY=188.889 StartZ=0 EndX=115 EndY=188 EndZ=0
    g80: LineSegment StartX=115.591 StartY=268.025 StartZ=0 EndX=113.5 EndY=268.025 EndZ=0
    g81: ArcOfCircle CenterX=113.4 CenterY=189.247 CenterZ=0 NormalX=0 NormalY=0 NormalZ=1 AngleXU=-1e-16 Radius=0.4 StartAngle=3.14159 EndAngle=4.24874
    g82: ArcOfCircle CenterX=115.765 CenterY=267.925 CenterZ=0 NormalX=0 NormalY=0 NormalZ=1 AngleXU=3.14159 Radius=0.200333 StartAngle=2.0944 EndAngle=5.75959
    g83: LineSegment StartX=113 StartY=189.247 StartZ=0 EndX=113 EndY=191.4 EndZ=0
    g84: LineSegment StartX=115.865 StartY=258.349 StartZ=0 EndX=115.865 EndY=267.751 EndZ=0
    g85: ArcOfCircle CenterX=113.4 CenterY=191.4 CenterZ=0 NormalX=0 NormalY=0 NormalZ=1 AngleXU=-1e-16 Radius=0.4 StartAngle=1.5708 EndAngle=3.14159
    g86: ArcOfCircle CenterX=115.765 CenterY=258.175 CenterZ=0 NormalX=0 NormalY=0 NormalZ=1 AngleXU=3.14159 Radius=0.200333 StartAngle=0.523599 EndAngle=4.18879
    g87: LineSegment StartX=113.4 StartY=191.8 StartZ=0 EndX=127 EndY=191.8 EndZ=0
    g88: LineSegment StartX=115.591 StartY=258.075 StartZ=0 EndX=113.5 EndY=258.075 EndZ=0
    g89: ArcOfCircle CenterX=127 CenterY=192.2 CenterZ=0 NormalX=0 NormalY=0 NormalZ=1 AngleXU=-1e-16 Radius=0.4 StartAngle=4.71239 EndAngle=7.85398
    g90: LineSegment StartX=113 StartY=257.575 StartZ=0 EndX=113.5 EndY=258.075 EndZ=0
    g91: LineSegment StartX=127 StartY=192.6 StartZ=0 EndX=113.4 EndY=192.6 EndZ=0
    g92: ArcOfCircle CenterX=113.4 CenterY=193 CenterZ=0 NormalX=0 NormalY=0 NormalZ=1 AngleXU=-1e-16 Radius=0.4 StartAngle=3.14159 EndAngle=4.71239
    g93: LineSegment StartX=113.5 StartY=220.525 StartZ=0 EndX=113 EndY=221.025 EndZ=0
    g94: LineSegment StartX=113 StartY=193 StartZ=0 EndX=113 EndY=210.075 EndZ=0
    g95: LineSegment StartX=115.591 StartY=220.525 StartZ=0 EndX=113.5 EndY=220.525 EndZ=0
    g96: LineSegment StartX=113 StartY=210.075 StartZ=0 EndX=113.5 EndY=210.575 EndZ=0
    g97: ArcOfCircle CenterX=115.765 CenterY=220.425 CenterZ=0 NormalX=0 NormalY=0 NormalZ=1 AngleXU=3.14159 Radius=0.200333 StartAngle=2.0944 EndAngle=5.75959
    g98: LineSegment StartX=115.591 StartY=210.575 StartZ=0 EndX=113.5 EndY=210.575 EndZ=0
    g99: LineSegment StartX=115.865 StartY=210.849 StartZ=0 EndX=115.865 EndY=220.251 EndZ=0
    g100: ArcOfCircle CenterX=115.765 CenterY=210.675 CenterZ=0 NormalX=0 NormalY=0 NormalZ=1 AngleXU=3.14159 Radius=0.200333 StartAngle=0.523599 EndAngle=4.18879
    g101: ArcOfCircle CenterX=167.19 CenterY=208.4 CenterZ=0 NormalX=0 NormalY=0 NormalZ=1 AngleXU=-1e-16 Radius=0.8 StartAngle=5.95649 EndAngle=9.11749
    g102: ArcOfCircle CenterX=190.8 CenterY=200.4 CenterZ=0 NormalX=0 NormalY=0 NormalZ=1 AngleXU=-1e-16 Radius=24.1285 StartAngle=2.81489 EndAngle=3.46829
    g103: ArcOfCircle CenterX=192.4 CenterY=200.4 CenterZ=0 NormalX=0 NormalY=0 NormalZ=1 AngleXU=-1e-16 Radius=27.2489 StartAngle=2.83431 EndAngle=3.44888
    g104: ArcOfCircle CenterX=167.19 CenterY=192.4 CenterZ=0 NormalX=0 NormalY=0 NormalZ=1 AngleXU=-1e-16 Radius=0.8 StartAngle=3.44888 EndAngle=6.60988
    g105: ArcOfCircle CenterX=139.41 CenterY=193.71 CenterZ=0 NormalX=0 NormalY=0 NormalZ=1 AngleXU=-1e-16 Radius=2.11 StartAngle=2.88608 EndAngle=4.71239
    g106: ArcOfCircle CenterX=113.8 CenterY=200.4 CenterZ=0 NormalX=0 NormalY=0 NormalZ=1 AngleXU=-1e-16 Radius=24.3594 StartAngle=6.02767 EndAngle=6.5387
    g107: LineSegment StartX=139.41 StartY=191.6 StartZ=0 EndX=162.19 EndY=191.6 EndZ=0
    g108: ArcOfCircle CenterX=139.41 CenterY=207.09 CenterZ=0 NormalX=0 NormalY=0 NormalZ=1 AngleXU=-1e-16 Radius=2.11 StartAngle=1.5708 EndAngle=3.39711
    g109: ArcOfCircle CenterX=162.19 CenterY=193.71 CenterZ=0 NormalX=0 NormalY=0 NormalZ=1 AngleXU=-1e-16 Radius=2.11 StartAngle=4.71239 EndAngle=6.5387
    g110: LineSegment StartX=162.19 StartY=209.2 StartZ=0 EndX=139.41 EndY=209.2 EndZ=0
    g111: ArcOfCircle CenterX=187.8 CenterY=200.4 CenterZ=0 NormalX=0 NormalY=0 NormalZ=1 AngleXU=-1e-16 Radius=24.3594 StartAngle=2.88608 EndAngle=3.39711
    g112: ArcOfCircle CenterX=162.19 CenterY=207.09 CenterZ=0 NormalX=0 NormalY=0 NormalZ=1 AngleXU=-1e-16 Radius=2.11 StartAngle=6.02767 EndAngle=7.85398
    g113: ArcOfCircle CenterX=134.41 CenterY=208.4 CenterZ=0 NormalX=0 NormalY=0 NormalZ=1 AngleXU=-1e-16 Radius=0.8 StartAngle=0.307283 EndAngle=3.46829
    g114: ArcOfCircle CenterX=109.2 CenterY=200.4 CenterZ=0 NormalX=0 NormalY=0 NormalZ=1 AngleXU=-1e-16 Radius=27.2489 StartAngle=5.9759 EndAngle=6.59047
    g115: ArcOfCircle CenterX=110.8 CenterY=200.4 CenterZ=0 NormalX=0 NormalY=0 NormalZ=1 AngleXU=-1e-16 Radius=24.1285 StartAngle=5.95649 EndAngle=6.60988
    g116: ArcOfCircle CenterX=134.41 CenterY=192.4 CenterZ=0 NormalX=0 NormalY=0 NormalZ=1 AngleXU=-1e-16 Radius=0.8 StartAngle=2.81489 EndAngle=5.9759
    g117: LineSegment StartX=113 StartY=240.322 StartZ=0 EndX=113 EndY=257.575 EndZ=0
    g118: LineSegment StartX=113 StartY=239.322 StartZ=0 EndX=113 EndY=221.025 EndZ=0
    g119: LineSegment StartX=188.6 StartY=239.322 StartZ=0 EndX=188.6 EndY=221.025 EndZ=0
    g120: LineSegment StartX=188.6 StartY=239.322 StartZ=0 EndX=188.6 EndY=239.322 EndZ=0
    g121: LineSegment StartX=113 StartY=287.2 StartZ=0 EndX=113 EndY=285.6 EndZ=0
    g122: LineSegment StartX=188.6 StartY=287.2 StartZ=0 EndX=188.6 EndY=285.6 EndZ=0
    g123: LineSegment StartX=188.6 StartY=193 StartZ=0 EndX=188.6 EndY=191.4 EndZ=0
    g124: LineSegment StartX=113 StartY=193 StartZ=0 EndX=113 EndY=191.4 EndZ=0
  constraints (19):
    c: Coincident(g118,g93)
    c: Vertical(g118)
    c: Coincident(g119,g120)
    c: Coincident(g119,g21)
    c: Vertical(g119)
    c: PointOnObject(g120,g119)
    c: Coincident(g121,g64)
    c: Tangent(g121,g74) = -1.5708
    c: Vertical(g121)
    c: Tangent(g122,g10) = 1.5708
    c: Coincident(g122,g0)
    c: Vertical(g122)
    c: Coincident(g123,g39)
    c: Tangent(g123,g49) = 1.5708
    c: Vertical(g123)
    c: Coincident(g124,g92)
    c: Coincident(g124,g83)
    c: Vertical(g124)
    c: Tangent(g124,g85)
FEATURE [Sketcher::SketchObject] Sketch009
  ArcFitTolerance = 1e-06
  FullyConstrained = false
  MakeInternals = false
  sketch-geometry (142):
    g0: LineSegment StartX=133.985 StartY=121 StartZ=0 EndX=125.317 EndY=121 EndZ=0
    g1: LineSegment StartX=133.985 StartY=121 StartZ=0 EndX=134.485 EndY=121.5 EndZ=0
    g2: ArcOfCircle CenterX=125.317 CenterY=120.6 CenterZ=0 NormalX=0 NormalY=0 NormalZ=1 AngleXU=1.5708 Radius=0.4 StartAngle=0 EndAngle=0.261799
    g3: LineSegment StartX=134.485 StartY=121.5 StartZ=0 EndX=134.485 EndY=123.591 EndZ=0
    g4: LineSegment StartX=125.213 StartY=120.986 StartZ=0 EndX=117.8 EndY=119 EndZ=0
    g5: ArcOfCircle CenterX=134.585 CenterY=123.765 CenterZ=0 NormalX=0 NormalY=0 NormalZ=1 AngleXU=1.5708 Radius=0.200333 StartAngle=0 EndAngle=2.61799
    g6: LineSegment StartX=117.8 StartY=119 StartZ=0 EndX=117.8 EndY=121 EndZ=0
    g7: ArcOfCircle CenterX=134.585 CenterY=123.765 CenterZ=0 NormalX=0 NormalY=0 NormalZ=1 AngleXU=1.5708 Radius=0.200333 StartAngle=5.23599 EndAngle=6.28319
    g8: LineSegment StartX=117.8 StartY=121 StartZ=0 EndX=115 EndY=121 EndZ=0
    g9: LineSegment StartX=134.759 StartY=123.865 StartZ=0 EndX=144.161 EndY=123.865 EndZ=0
    g10: LineSegment StartX=115 StartY=120 StartZ=0 EndX=115 EndY=121 EndZ=0
    g11: ArcOfCircle CenterX=144.335 CenterY=123.765 CenterZ=0 NormalX=0 NormalY=0 NormalZ=1 AngleXU=1.5708 Radius=0.200333 StartAngle=0 EndAngle=1.0472
    g12: LineSegment StartX=113.221 StartY=120.889 StartZ=0 EndX=115 EndY=120 EndZ=0
    g13: ArcOfCircle CenterX=144.335 CenterY=123.765 CenterZ=0 NormalX=0 NormalY=0 NormalZ=1 AngleXU=1.5708 Radius=0.200333 StartAngle=3.66519 EndAngle=6.28319
    g14: ArcOfCircle CenterX=113.4 CenterY=121.247 CenterZ=0 NormalX=0 NormalY=0 NormalZ=1 AngleXU=1.5708 Radius=0.4 StartAngle=1.5708 EndAngle=2.67795
    g15: LineSegment StartX=144.435 StartY=121.5 StartZ=0 EndX=144.435 EndY=123.591 EndZ=0
    g16: LineSegment StartX=113 StartY=121.247 StartZ=0 EndX=113 EndY=123.4 EndZ=0
    g17: LineSegment StartX=144.435 StartY=121.5 StartZ=0 EndX=144.935 EndY=121 EndZ=0
    g18: ArcOfCircle CenterX=113.4 CenterY=123.4 CenterZ=0 NormalX=0 NormalY=0 NormalZ=1 AngleXU=1.5708 Radius=0.4 StartAngle=0 EndAngle=1.5708
    g19: LineSegment StartX=156.665 StartY=121 StartZ=0 EndX=144.935 EndY=121 EndZ=0
    g20: LineSegment StartX=113.4 StartY=123.8 StartZ=0 EndX=127 EndY=123.8 EndZ=0
    g21: LineSegment StartX=156.665 StartY=121 StartZ=0 EndX=157.165 EndY=121.5 EndZ=0
    g22: ArcOfCircle CenterX=127 CenterY=124.2 CenterZ=0 NormalX=0 NormalY=0 NormalZ=1 AngleXU=0 Radius=0.4 StartAngle=4.71239 EndAngle=7.85398
    g23: LineSegment StartX=157.165 StartY=121.5 StartZ=0 EndX=157.165 EndY=123.591 EndZ=0
    g24: LineSegment StartX=127 StartY=124.6 StartZ=0 EndX=113.4 EndY=124.6 EndZ=0
    g25: ArcOfCircle CenterX=157.265 CenterY=123.765 CenterZ=0 NormalX=0 NormalY=0 NormalZ=1 AngleXU=1.5708 Radius=0.200333 StartAngle=0 EndAngle=2.61799
    g26: ArcOfCircle CenterX=113.4 CenterY=125 CenterZ=0 NormalX=0 NormalY=0 NormalZ=1 AngleXU=1.5708 Radius=0.4 StartAngle=1.5708 EndAngle=3.14159
    g27: ArcOfCircle CenterX=157.265 CenterY=123.765 CenterZ=0 NormalX=0 NormalY=0 NormalZ=1 AngleXU=1.5708 Radius=0.200333 StartAngle=5.23599 EndAngle=6.28319
    g28: LineSegment StartX=113 StartY=125 StartZ=0 EndX=113 EndY=135.825 EndZ=0
    g29: LineSegment StartX=157.439 StartY=123.865 StartZ=0 EndX=166.841 EndY=123.865 EndZ=0
    g30: LineSegment StartX=113.5 StartY=136.325 StartZ=0 EndX=113 EndY=135.825 EndZ=0
    g31: ArcOfCircle CenterX=167.015 CenterY=123.765 CenterZ=0 NormalX=0 NormalY=0 NormalZ=1 AngleXU=1.5708 Radius=0.200333 StartAngle=0 EndAngle=1.0472
    g32: LineSegment StartX=113.5 StartY=136.325 StartZ=0 EndX=115.591 EndY=136.325 EndZ=0
    g33: ArcOfCircle CenterX=167.015 CenterY=123.765 CenterZ=0 NormalX=0 NormalY=0 NormalZ=1 AngleXU=1.5708 Radius=0.200333 StartAngle=3.66519 EndAngle=6.28319
    g34: ArcOfCircle CenterX=115.765 CenterY=136.425 CenterZ=0 NormalX=0 NormalY=0 NormalZ=1 AngleXU=0 Radius=0.200333 StartAngle=3.66519 EndAngle=6.28319
    g35: LineSegment StartX=167.115 StartY=121.5 StartZ=0 EndX=167.115 EndY=123.591 EndZ=0
    g36: ArcOfCircle CenterX=115.765 CenterY=136.425 CenterZ=0 NormalX=0 NormalY=0 NormalZ=1 AngleXU=0 Radius=0.200333 StartAngle=0 EndAngle=1.0472
    g37: LineSegment StartX=167.115 StartY=121.5 StartZ=0 EndX=167.615 EndY=121 EndZ=0
    g38: LineSegment StartX=115.865 StartY=146.001 StartZ=0 EndX=115.865 EndY=141.777 EndZ=0
    g39: LineSegment StartX=176.283 StartY=121 StartZ=0 EndX=167.615 EndY=121 EndZ=0
    g40: ArcOfCircle CenterX=115.765 CenterY=146.175 CenterZ=0 NormalX=0 NormalY=0 NormalZ=1 AngleXU=0 Radius=0.200333 StartAngle=5.23599 EndAngle=6.28319
    g41: ArcOfCircle CenterX=176.283 CenterY=120.6 CenterZ=0 NormalX=0 NormalY=0 NormalZ=1 AngleXU=1.5708 Radius=0.4 StartAngle=6.02139 EndAngle=6.28319
    g42: ArcOfCircle CenterX=115.765 CenterY=146.175 CenterZ=0 NormalX=0 NormalY=0 NormalZ=1 AngleXU=0 Radius=0.200333 StartAngle=0 EndAngle=2.61799
    g43: LineSegment StartX=183.8 StartY=119 StartZ=0 EndX=176.387 EndY=120.986 EndZ=0
    g44: LineSegment StartX=113.5 StartY=146.275 StartZ=0 EndX=115.591 EndY=146.275 EndZ=0
    g45: LineSegment StartX=183.8 StartY=121 StartZ=0 EndX=183.8 EndY=119 EndZ=0
    g46: LineSegment StartX=113 StartY=146.775 StartZ=0 EndX=113.5 EndY=146.275 EndZ=0
    g47: LineSegment StartX=186.6 StartY=121 StartZ=0 EndX=183.8 EndY=121 EndZ=0
    g48: LineSegment StartX=186.6 StartY=120 StartZ=0 EndX=186.6 EndY=121 EndZ=0
    g49: ArcOfCircle CenterX=113.4 CenterY=157.6 CenterZ=0 NormalX=0 NormalY=0 NormalZ=1 AngleXU=1.5708 Radius=0.4 StartAngle=0 EndAngle=1.5708
    g50: LineSegment StartX=188.379 StartY=120.889 StartZ=0 EndX=186.6 EndY=120 EndZ=0
    g51: LineSegment StartX=113.4 StartY=158 StartZ=0 EndX=127 EndY=158 EndZ=0
    g52: ArcOfCircle CenterX=188.2 CenterY=121.247 CenterZ=0 NormalX=0 NormalY=0 NormalZ=1 AngleXU=1.5708 Radius=0.4 StartAngle=3.60524 EndAngle=4.71239
    g53: ArcOfCircle CenterX=127 CenterY=158.4 CenterZ=0 NormalX=0 NormalY=0 NormalZ=1 AngleXU=0 Radius=0.4 StartAngle=4.71239 EndAngle=7.85398
    g54: LineSegment StartX=188.6 StartY=123.4 StartZ=0 EndX=188.6 EndY=121.247 EndZ=0
    g55: LineSegment StartX=127 StartY=158.8 StartZ=0 EndX=113.4 EndY=158.8 EndZ=0
    g56: ArcOfCircle CenterX=188.2 CenterY=123.4 CenterZ=0 NormalX=0 NormalY=0 NormalZ=1 AngleXU=1.5708 Radius=0.4 StartAngle=4.71239 EndAngle=6.28319
    g57: ArcOfCircle CenterX=113.4 CenterY=159.2 CenterZ=0 NormalX=0 NormalY=0 NormalZ=1 AngleXU=1.5708 Radius=0.4 StartAngle=1.5708 EndAngle=3.14159
    g58: LineSegment StartX=174.6 StartY=123.8 StartZ=0 EndX=188.2 EndY=123.8 EndZ=0
    g59: LineSegment StartX=113 StartY=159.2 StartZ=0 EndX=113 EndY=161.353 EndZ=0
    g60: ArcOfCircle CenterX=174.6 CenterY=124.2 CenterZ=0 NormalX=0 NormalY=0 NormalZ=1 AngleXU=0 Radius=0.4 StartAngle=1.5708 EndAngle=4.71239
    g61: ArcOfCircle CenterX=113.4 CenterY=161.353 CenterZ=0 NormalX=0 NormalY=0 NormalZ=1 AngleXU=1.5708 Radius=0.4 StartAngle=0.463648 EndAngle=1.5708
    g62: LineSegment StartX=188.2 StartY=124.6 StartZ=0 EndX=174.6 EndY=124.6 EndZ=0
    g63: LineSegment StartX=113.221 StartY=161.711 StartZ=0 EndX=115 EndY=162.6 EndZ=0
    g64: ArcOfCircle CenterX=188.2 CenterY=125 CenterZ=0 NormalX=0 NormalY=0 NormalZ=1 AngleXU=1.5708 Radius=0.4 StartAngle=3.14159 EndAngle=4.71239
    g65: LineSegment StartX=115 StartY=162.6 StartZ=0 EndX=115 EndY=161.6 EndZ=0
    g66: LineSegment StartX=188.6 StartY=135.825 StartZ=0 EndX=188.6 EndY=125 EndZ=0
    g67: LineSegment StartX=115 StartY=161.6 StartZ=0 EndX=117.8 EndY=161.6 EndZ=0
    g68: LineSegment StartX=188.6 StartY=135.825 StartZ=0 EndX=188.1 EndY=136.325 EndZ=0
    g69: LineSegment StartX=117.8 StartY=161.6 StartZ=0 EndX=117.8 EndY=163.6 EndZ=0
    g70: LineSegment StartX=186.009 StartY=136.325 StartZ=0 EndX=188.1 EndY=136.325 EndZ=0
    g71: LineSegment StartX=117.8 StartY=163.6 StartZ=0 EndX=125.213 EndY=161.614 EndZ=0
    g72: ArcOfCircle CenterX=185.835 CenterY=136.425 CenterZ=0 NormalX=0 NormalY=0 NormalZ=1 AngleXU=0 Radius=0.200333 StartAngle=2.0944 EndAngle=5.75959
    g73: ArcOfCircle CenterX=125.317 CenterY=162 CenterZ=0 NormalX=0 NormalY=0 NormalZ=1 AngleXU=1.5708 Radius=0.4 StartAngle=2.87979 EndAngle=3.14159
    g74: LineSegment StartX=185.735 StartY=146.001 StartZ=0 EndX=185.735 EndY=141.777 EndZ=0
    g75: LineSegment StartX=125.317 StartY=161.6 StartZ=0 EndX=133.985 EndY=161.6 EndZ=0
    g76: ArcOfCircle CenterX=185.835 CenterY=146.175 CenterZ=0 NormalX=0 NormalY=0 NormalZ=1 AngleXU=0 Radius=0.200333 StartAngle=0.523599 EndAngle=4.18879
    g77: LineSegment StartX=134.485 StartY=161.1 StartZ=0 EndX=133.985 EndY=161.6 EndZ=0
    g78: LineSegment StartX=186.009 StartY=146.275 StartZ=0 EndX=188.1 EndY=146.275 EndZ=0
    g79: LineSegment StartX=134.485 StartY=161.1 StartZ=0 EndX=134.485 EndY=159.009 EndZ=0
    g80: LineSegment StartX=188.1 StartY=146.275 StartZ=0 EndX=188.6 EndY=146.775 EndZ=0
    g81: ArcOfCircle CenterX=134.585 CenterY=158.835 CenterZ=0 NormalX=0 NormalY=0 NormalZ=1 AngleXU=-1.5708 Radius=0.200333 StartAngle=3.66519 EndAngle=6.28319
    g82: ArcOfCircle CenterX=134.585 CenterY=158.835 CenterZ=0 NormalX=0 NormalY=0 NormalZ=1 AngleXU=-1.5708 Radius=0.200333 StartAngle=0 EndAngle=1.0472
    g83: ArcOfCircle CenterX=188.2 CenterY=157.6 CenterZ=0 NormalX=0 NormalY=0 NormalZ=1 AngleXU=1.5708 Radius=0.4 StartAngle=4.71239 EndAngle=6.28319
    g84: LineSegment StartX=144.161 StartY=158.735 StartZ=0 EndX=134.759 EndY=158.735 EndZ=0
    g85: LineSegment StartX=174.6 StartY=158 StartZ=0 EndX=188.2 EndY=158 EndZ=0
    g86: ArcOfCircle CenterX=144.335 CenterY=158.835 CenterZ=0 NormalX=0 NormalY=0 NormalZ=1 AngleXU=-1.5708 Radius=0.200333 StartAngle=5.23599 EndAngle=6.28319
    g87: ArcOfCircle CenterX=174.6 CenterY=158.4 CenterZ=0 NormalX=0 NormalY=0 NormalZ=1 AngleXU=0 Radius=0.4 StartAngle=1.5708 EndAngle=4.71239
    g88: ArcOfCircle CenterX=144.335 CenterY=158.835 CenterZ=0 NormalX=0 NormalY=0 NormalZ=1 AngleXU=-1.5708 Radius=0.200333 StartAngle=0 EndAngle=2.61799
    g89: LineSegment StartX=188.2 StartY=158.8 StartZ=0 EndX=174.6 EndY=158.8 EndZ=0
    g90: LineSegment StartX=144.435 StartY=161.1 StartZ=0 EndX=144.435 EndY=159.009 EndZ=0
    g91: ArcOfCircle CenterX=188.2 CenterY=159.2 CenterZ=0 NormalX=0 NormalY=0 NormalZ=1 AngleXU=1.5708 Radius=0.4 StartAngle=3.14159 EndAngle=4.71239
    g92: LineSegment StartX=144.935 StartY=161.6 StartZ=0 EndX=144.435 EndY=161.1 EndZ=0
    g93: LineSegment StartX=188.6 StartY=161.353 StartZ=0 EndX=188.6 EndY=159.2 EndZ=0
    g94: LineSegment StartX=144.935 StartY=161.6 StartZ=0 EndX=156.665 EndY=161.6 EndZ=0
    g95: ArcOfCircle CenterX=188.2 CenterY=161.353 CenterZ=0 NormalX=0 NormalY=0 NormalZ=1 AngleXU=1.5708 Radius=0.4 StartAngle=4.71239 EndAngle=5.81954
    g96: LineSegment StartX=157.165 StartY=161.1 StartZ=0 EndX=156.665 EndY=161.6 EndZ=0
    g97: LineSegment StartX=188.379 StartY=161.711 StartZ=0 EndX=186.6 EndY=162.6 EndZ=0
    g98: LineSegment StartX=157.165 StartY=161.1 StartZ=0 EndX=157.165 EndY=159.009 EndZ=0
    g99: LineSegment StartX=186.6 StartY=161.6 StartZ=0 EndX=186.6 EndY=162.6 EndZ=0
    g100: ArcOfCircle CenterX=157.265 CenterY=158.835 CenterZ=0 NormalX=0 NormalY=0 NormalZ=1 AngleXU=-1.5708 Radius=0.200333 StartAngle=3.66519 EndAngle=6.28319
    g101: LineSegment StartX=183.8 StartY=161.6 StartZ=0 EndX=186.6 EndY=161.6 EndZ=0
    g102: ArcOfCircle CenterX=157.265 CenterY=158.835 CenterZ=0 NormalX=0 NormalY=0 NormalZ=1 AngleXU=-1.5708 Radius=0.200333 StartAngle=0 EndAngle=1.0472
    g103: LineSegment StartX=183.8 StartY=163.6 StartZ=0 EndX=183.8 EndY=161.6 EndZ=0
    g104: LineSegment StartX=166.841 StartY=158.735 StartZ=0 EndX=157.439 EndY=158.735 EndZ=0
    g105: LineSegment StartX=176.387 StartY=161.614 StartZ=0 EndX=183.8 EndY=163.6 EndZ=0
    g106: ArcOfCircle CenterX=167.015 CenterY=158.835 CenterZ=0 NormalX=0 NormalY=0 NormalZ=1 AngleXU=-1.5708 Radius=0.200333 StartAngle=5.23599 EndAngle=6.28319
    g107: ArcOfCircle CenterX=176.283 CenterY=162 CenterZ=0 NormalX=0 NormalY=0 NormalZ=1 AngleXU=1.5708 Radius=0.4 StartAngle=3.14159 EndAngle=3.40339
    g108: ArcOfCircle CenterX=167.015 CenterY=158.835 CenterZ=0 NormalX=0 NormalY=0 NormalZ=1 AngleXU=-1.5708 Radius=0.200333 StartAngle=0 EndAngle=2.61799
    g109: LineSegment StartX=167.615 StartY=161.6 StartZ=0 EndX=176.283 EndY=161.6 EndZ=0
    g110: LineSegment StartX=167.115 StartY=161.1 StartZ=0 EndX=167.115 EndY=159.009 EndZ=0
    g111: LineSegment StartX=167.615 StartY=161.6 StartZ=0 EndX=167.115 EndY=161.1 EndZ=0
    g112: Circle CenterX=138 CenterY=134.3 CenterZ=0 NormalX=0 NormalY=0 NormalZ=1 AngleXU=0 Radius=8.5
    g113: LineSegment StartX=147.95 StartY=128.7 StartZ=0 EndX=153.65 EndY=128.7 EndZ=0
    g114: ArcOfCircle CenterX=147.95 CenterY=126.2 CenterZ=0 NormalX=0 NormalY=0 NormalZ=1 AngleXU=0 Radius=2.5 StartAngle=1.5708 EndAngle=4.71239
    g115: ArcOfCircle CenterX=153.65 CenterY=126.2 CenterZ=0 NormalX=0 NormalY=0 NormalZ=1 AngleXU=0 Radius=2.5 StartAngle=4.71239 EndAngle=7.85398
    g116: LineSegment StartX=147.95 StartY=123.7 StartZ=0 EndX=153.65 EndY=123.7 EndZ=0
    g117: LineSegment StartX=126.8 StartY=153.91 StartZ=0 EndX=138.8 EndY=153.91 EndZ=0
    g118: ArcOfCircle CenterX=126.8 CenterY=153.155 CenterZ=0 NormalX=0 NormalY=0 NormalZ=1 AngleXU=0 Radius=0.755 StartAngle=1.5708 EndAngle=4.71239
    g119: ArcOfCircle CenterX=138.8 CenterY=153.155 CenterZ=0 NormalX=0 NormalY=0 NormalZ=1 AngleXU=0 Radius=0.755 StartAngle=4.71239 EndAngle=7.85398
    g120: LineSegment StartX=126.8 StartY=152.4 StartZ=0 EndX=138.8 EndY=152.4 EndZ=0
    g121: Circle CenterX=163.6 CenterY=134.3 CenterZ=0 NormalX=0 NormalY=0 NormalZ=1 AngleXU=0 Radius=8.5
    g122: LineSegment StartX=162.8 StartY=153.91 StartZ=0 EndX=174.8 EndY=153.91 EndZ=0
    g123: ArcOfCircle CenterX=162.8 CenterY=153.155 CenterZ=0 NormalX=0 NormalY=0 NormalZ=1 AngleXU=0 Radius=0.755 StartAngle=1.5708 EndAngle=4.71239
    g124: ArcOfCircle CenterX=174.8 CenterY=153.155 CenterZ=0 NormalX=0 NormalY=0 NormalZ=1 AngleXU=0 Radius=0.755 StartAngle=4.71239 EndAngle=7.85398
    g125: LineSegment StartX=162.8 StartY=152.4 StartZ=0 EndX=174.8 EndY=152.4 EndZ=0
    g126: LineSegment StartX=115.865 StartY=140.777 StartZ=0 EndX=115.865 EndY=136.599 EndZ=0
    g127: LineSegment StartX=185.735 StartY=140.777 StartZ=0 EndX=185.735 EndY=136.599 EndZ=0
    g128: LineSegment StartX=115.865 StartY=140.777 StartZ=0 EndX=115.865 EndY=141.777 EndZ=0
    g129: LineSegment StartX=185.735 StartY=140.777 StartZ=0 EndX=185.735 EndY=141.777 EndZ=0
    g130: LineSegment StartX=113 StartY=157.6 StartZ=0 EndX=113 EndY=148.605 EndZ=0
    g131: LineSegment StartX=113 StartY=147.608 StartZ=0 EndX=113 EndY=146.775 EndZ=0
    g132: LineSegment StartX=188.6 StartY=157.6 StartZ=0 EndX=188.6 EndY=148.601 EndZ=0
    g133: LineSegment StartX=188.6 StartY=147.602 StartZ=0 EndX=188.6 EndY=146.775 EndZ=0
    g134: LineSegment StartX=113 StartY=159.2 StartZ=0 EndX=113 EndY=157.6 EndZ=0
    g135: LineSegment StartX=188.6 StartY=159.2 StartZ=0 EndX=188.6 EndY=157.6 EndZ=0
    g136: LineSegment StartX=188.6 StartY=125 StartZ=0 EndX=188.6 EndY=123.4 EndZ=0
    g137: LineSegment StartX=113 StartY=125 StartZ=0 EndX=113 EndY=123.4 EndZ=0
    g138: LineSegment [constr] StartX=138 StartY=134.3 StartZ=0 EndX=150.8 EndY=134.3 EndZ=0
    g139: LineSegment [constr] StartX=150.8 StartY=134.3 StartZ=0 EndX=163.6 EndY=134.3 EndZ=0
    g140: LineSegment [constr] StartX=147.95 StartY=126.2 StartZ=0 EndX=153.65 EndY=126.2 EndZ=0
    g141: LineSegment [constr] StartX=150.8 StartY=126.2 StartZ=0 EndX=150.8 EndY=134.3 EndZ=0
  constraints (44):
    c: Coincident(g128,g126)
    c: Coincident(g128,g38)
    c: Vertical(g128)
    c: Coincident(g129,g127)
    c: Coincident(g129,g74)
    c: Vertical(g129)
    c: Coincident(g130,g49)
    c: Vertical(g130)
    c: Coincident(g131,g46)
    c: Vertical(g131)
    c: Tangent(g132,g83) = 1.5708
    c: Vertical(g132)
    c: Coincident(g133,g80)
    c: Vertical(g133)
    c: Coincident(g134,g57)
    c: Tangent(g134,g49) = -1.5708
    c: Vertical(g134)
    c: Coincident(g135,g91)
    c: Tangent(g135,g83) = 1.5708
    c: Tangent(g136,g64) = 1.5708
    c: Coincident(g136,g54)
    c: Vertical(g136)
    c: Tangent(g137,g26) = -1.5708
    c: Coincident(g137,g16)
    c: Vertical(g137)
    c: DistanceX(g112) = 138
    c: DistanceY(g112) = 134.3
    c: Diameter(g112) = 17
    c: DistanceX(g114) = 147.95
    c: DistanceY(g114) = 126.2
    c: DistanceX(g115) = 153.65
    c: DistanceY(g115) = 126.2
    c: Coincident(g138,g112)
    c: Horizontal(g138)
    c: Coincident(g139,g138)
    c: Coincident(g139,g121)
    c: Coincident(g140,g114)
    c: Coincident(g140,g115)
    c: Symmetric(g140,g140,g141)
    c: Coincident(g141,g138)
    c: Vertical(g141)
    c: Horizontal(g139)
    c: Equal(g138,g139)
    c: Equal(g121,g112)
